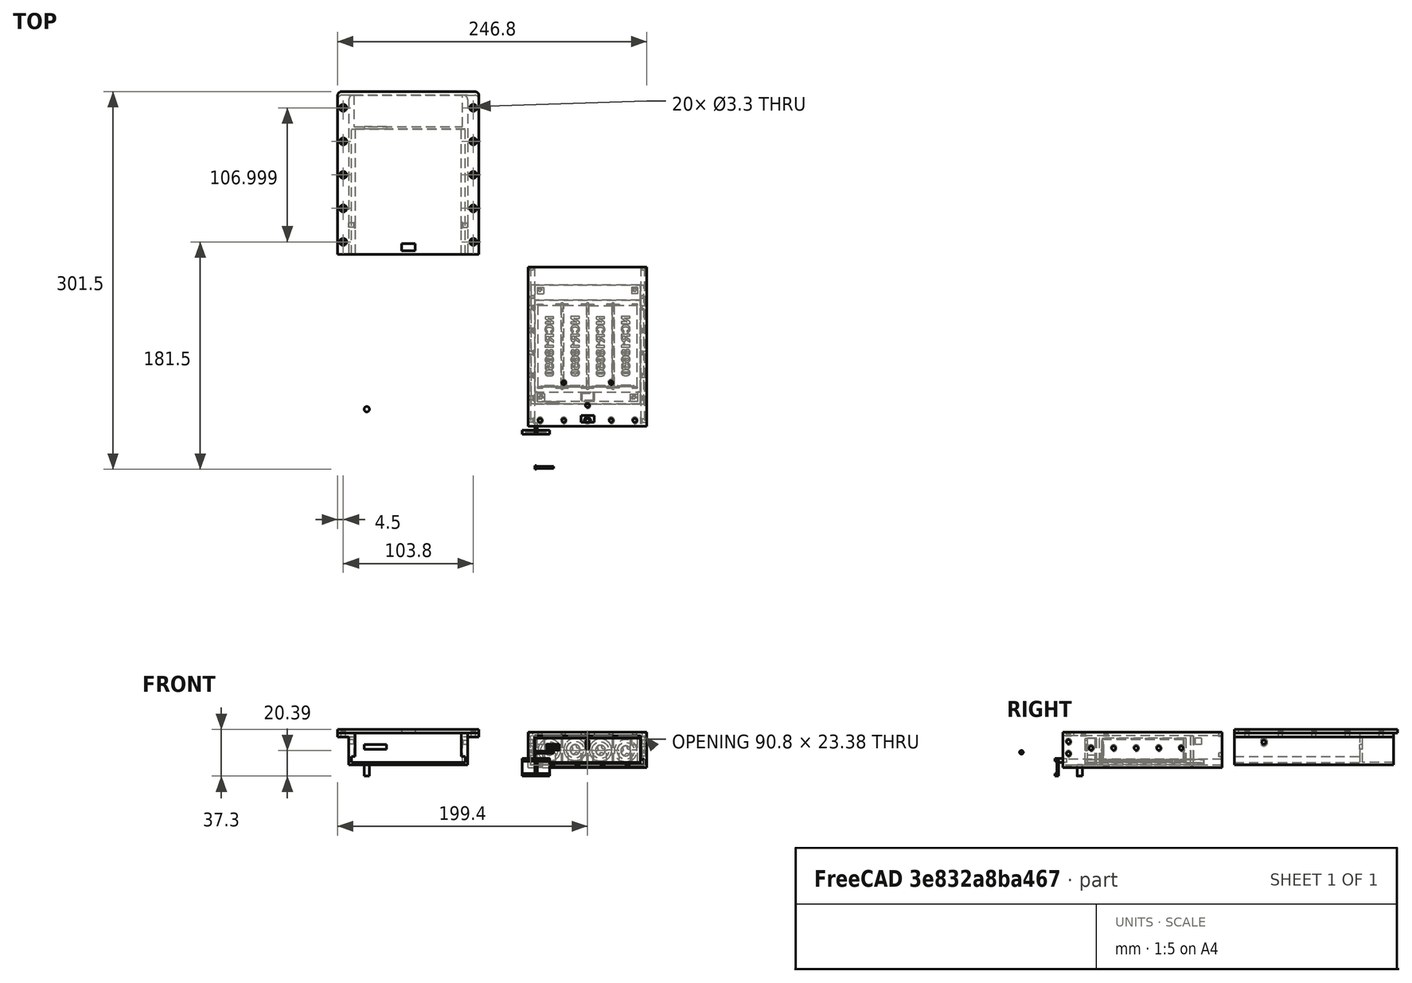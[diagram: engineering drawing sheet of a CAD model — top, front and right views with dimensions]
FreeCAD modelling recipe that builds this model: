
FCSTD DOCUMENT  (FreeCAD 0.21R33771 (Git))
Label: Final Battery Design
License: All rights reserved
LicenseURL: http://en.wikipedia.org/wiki/All_rights_reserved
objects: Sketcher::SketchObject×66, Part::Extrusion×27, App::MeasureDistance×25, PartDesign::Hole×17, PartDesign::Pocket×16, App::Part×14, PartDesign::Body×10, PartDesign::FeatureBase×10, Part::Feature×4, PartDesign::Pad×4, PartDesign::Fillet×3, TechDraw::DrawViewDimension×2, TechDraw::DrawSVGTemplate×1, TechDraw::DrawViewPart×1, TechDraw::DrawPage×1
note: 199 computed .brp shape members not serialized (recipe doc carries the construction recipe); baked Part::Feature solids carry a one-line shape summary decoded from their .brp

FEATURE [Part::Feature] Part__Feature  label="cell 001"
  Placement = pos=(11.67,-30.7,11.73) rot=(1,0,0;1.5708rad)
  shape: bbox 19.48 x 65 x 19.48 mm, 202 faces (baked)
FEATURE [Part::Feature] Part__Feature001  label="cell 002"
  Placement = pos=(32.21,-30.56,12.09) rot=(1,0,0;1.5708rad)
  shape: bbox 19.48 x 65 x 19.48 mm, 202 faces (baked)
FEATURE [Part::Feature] Part__Feature002  label="cell 003"
  Placement = pos=(52.45,-30.79,11.7) rot=(1,0,0;1.5708rad)
  shape: bbox 19.48 x 65 x 19.48 mm, 202 faces (baked)
FEATURE [Part::Feature] Part__Feature003  label="cell 004"
  Placement = pos=(72.58,-30.46,11.13) rot=(1,0,0;1.5708rad)
  shape: bbox 19.48 x 65 x 19.48 mm, 202 faces (baked)
FEATURE [PartDesign::Body] Body  label="CELL MOUNT BODY"
  Origin = -> Origin001
FEATURE [Sketcher::SketchObject] Sketch
  FullyConstrained = false
  MapMode = 5
  Support = -> [XY_Plane001]
  sketch-geometry (4):
    g0: LineSegment StartX=0 StartY=-99.794 StartZ=0 EndX=84.2 EndY=-99.794 EndZ=0
    g1: LineSegment StartX=84.2 StartY=-99.794 StartZ=0 EndX=84.2 EndY=-26.494 EndZ=0
    g2: LineSegment StartX=84.2 StartY=-26.494 StartZ=0 EndX=0 EndY=-26.494 EndZ=0
    g3: LineSegment StartX=0 StartY=-26.494 StartZ=0 EndX=0 EndY=-99.794 EndZ=0
  constraints (10):
    c: Coincident(g0,g1)
    c: Coincident(g1,g2)
    c: Coincident(g2,g3)
    c: Coincident(g3,g0)
    c: Horizontal(g0)
    c: Horizontal(g2)
    c: Vertical(g1)
    c: Vertical(g3)
    c: DistanceX(g2,g2) = 84.2
    c: DistanceY(g3,g3) = 73.3
FEATURE [App::Part] Part001  label="Batt Cells"
  Group = -> [Part__Feature,Part__Feature001,Part__Feature002,Part__Feature003]
  Origin = -> Origin002
FEATURE [Part::Extrusion] Extrude  label="CELL MOUNT FLOOR"
  Base = -> Sketch
  Dir = (0,0,1)
  DirMode = 2
  FaceMakerClass = Part::FaceMakerBullseye
  LengthFwd = 2
  LengthRev = 0
  Solid = true
  Symmetric = false
FEATURE [Sketcher::SketchObject] Sketch001
  FullyConstrained = false
  MapMode = 5
  Placement = pos=(0,0,2) rot=(0,0,1;0rad)
  Support = -> [Extrude]
  sketch-geometry (12):
    g0: LineSegment StartX=0 StartY=-26.494 StartZ=0 EndX=84.2 EndY=-26.494 EndZ=0
    g1: LineSegment StartX=84.2 StartY=-26.494 StartZ=0 EndX=84.2 EndY=-99.794 EndZ=0
    g2: LineSegment StartX=84.2 StartY=-99.794 StartZ=0 EndX=0 EndY=-99.794 EndZ=0
    g3: LineSegment StartX=0 StartY=-99.794 StartZ=0 EndX=0 EndY=-26.494 EndZ=0
    g4: LineSegment StartX=84.2 StartY=-99.794 StartZ=0 EndX=84.2 EndY=-97.79 EndZ=0
    g5: LineSegment StartX=84.2 StartY=-97.79 StartZ=0 EndX=82.2 EndY=-97.79 EndZ=0
    g6: LineSegment StartX=0 StartY=-26.494 StartZ=0 EndX=0 EndY=-28.49 EndZ=0
    g7: LineSegment StartX=0 StartY=-28.49 StartZ=0 EndX=2 EndY=-28.49 EndZ=0
    g8: LineSegment StartX=2 StartY=-28.49 StartZ=0 EndX=82.2 EndY=-28.49 EndZ=0
    g9: LineSegment StartX=82.2 StartY=-28.49 StartZ=0 EndX=82.2 EndY=-97.79 EndZ=0
    g10: LineSegment StartX=82.2 StartY=-97.79 StartZ=0 EndX=2 EndY=-97.79 EndZ=0
    g11: LineSegment StartX=2 StartY=-97.79 StartZ=0 EndX=2 EndY=-28.49 EndZ=0
  constraints (31):
    c: Coincident(g0,g1)
    c: Coincident(g1,g2)
    c: Coincident(g2,g3)
    c: Coincident(g3,g0)
    c: Horizontal(g0)
    c: Horizontal(g2)
    c: Vertical(g1)
    c: Vertical(g3)
    c: PointOnObject(g0,g-2)
    c: DistanceX(g2,g2) = 84.2
    c: DistanceY(g1,g1) = 73.3
    c: Coincident(g4,g1)
    c: PointOnObject(g4,g1)
    c: Coincident(g5,g4)
    c: Horizontal(g5)
    c: Coincident(g6,g0)
    c: PointOnObject(g6,g3)
    c: Coincident(g7,g6)
    c: Horizontal(g7)
    c: Coincident(g8,g9)
    c: Coincident(g9,g10)
    c: Coincident(g10,g11)
    c: Coincident(g11,g8)
    c: Horizontal(g8)
    c: Horizontal(g10)
    c: Vertical(g9)
    c: Vertical(g11)
    c: Coincident(g8,g7)
    c: Coincident(g9,g5)
    c: DistanceX(g8,g8) = 80.2
    c: DistanceY(g9,g9) = 69.3
FEATURE [Part::Extrusion] Extrude001  label="CELL MOUNT EXT WALLS"
  Base = -> Sketch001
  Dir = (0,0,1)
  DirMode = 2
  FaceMakerClass = Part::FaceMakerBullseye
  LengthFwd = 19.3
  LengthRev = 0
  Solid = true
  Symmetric = false
FEATURE [Sketcher::SketchObject] Sketch002
  FullyConstrained = false
  MapMode = 5
  Placement = pos=(0,0,2) rot=(0,0,1;0rad)
  Support = -> [Extrude]
  sketch-geometry (15):
    g0: LineSegment StartX=22.2999 StartY=-28.6 StartZ=0 EndX=41.5999 EndY=-28.6 EndZ=0
    g1: LineSegment StartX=21.2995 StartY=-28.49 StartZ=0 EndX=22.2995 EndY=-28.49 EndZ=0
    g2: LineSegment StartX=22.2995 StartY=-28.49 StartZ=0 EndX=22.2995 EndY=-97.8 EndZ=0
    g3: LineSegment StartX=22.2995 StartY=-97.8 StartZ=0 EndX=21.2995 EndY=-97.8 EndZ=0
    g4: LineSegment StartX=21.2995 StartY=-97.8 StartZ=0 EndX=21.2995 EndY=-28.49 EndZ=0
    g5: LineSegment StartX=41.6 StartY=-28.49 StartZ=0 EndX=42.6 EndY=-28.49 EndZ=0
    g6: LineSegment StartX=42.6 StartY=-28.49 StartZ=0 EndX=42.6 EndY=-97.79 EndZ=0
    g7: LineSegment StartX=42.6 StartY=-97.79 StartZ=0 EndX=41.6 EndY=-97.79 EndZ=0
    g8: LineSegment StartX=41.6 StartY=-97.79 StartZ=0 EndX=41.6 EndY=-28.49 EndZ=0
    g9: LineSegment StartX=42.6 StartY=-28.6021 StartZ=0 EndX=61.9 EndY=-28.6021 EndZ=0
    g10: LineSegment StartX=61.9 StartY=-28.49 StartZ=0 EndX=62.9 EndY=-28.49 EndZ=0
    g11: LineSegment StartX=62.9 StartY=-28.49 StartZ=0 EndX=62.9 EndY=-97.8 EndZ=0
    g12: LineSegment StartX=62.9 StartY=-97.8 StartZ=0 EndX=61.9 EndY=-97.8 EndZ=0
    g13: LineSegment StartX=61.9 StartY=-97.8 StartZ=0 EndX=61.9 EndY=-28.49 EndZ=0
    g14: LineSegment StartX=62.9 StartY=-28.601 StartZ=0 EndX=82.2 EndY=-28.601 EndZ=0
  constraints (38):
    c: Horizontal(g0)
    c: Coincident(g1,g2)
    c: Coincident(g2,g3)
    c: Coincident(g3,g4)
    c: Coincident(g4,g1)
    c: Horizontal(g1)
    c: Horizontal(g3)
    c: Vertical(g2)
    c: Vertical(g4)
    c: Coincident(g5,g6)
    c: Coincident(g6,g7)
    c: Coincident(g7,g8)
    c: Coincident(g8,g5)
    c: Horizontal(g5)
    c: Horizontal(g7)
    c: Vertical(g6)
    c: Vertical(g8)
    c: PointOnObject(g9,g6)
    c: Horizontal(g9)
    c: Coincident(g10,g11)
    c: Coincident(g11,g12)
    c: Coincident(g12,g13)
    c: Coincident(g13,g10)
    c: Horizontal(g10)
    c: Horizontal(g12)
    c: Vertical(g11)
    c: Vertical(g13)
    c: PointOnObject(g14,g11)
    c: Horizontal(g14)
    c: DistanceY(g4,g4) = 69.31
    c: DistanceY(g8,g8) = 69.3
    c: DistanceY(g13,g13) = 69.31
    c: DistanceX(g1,g1) = 1
    c: DistanceX(g0,g0) = 19.3
    c: DistanceX(g9,g9) = 19.3
    c: DistanceX(g5,g5) = 1
    c: DistanceX(g10,g10) = 1
    c: DistanceX(g14,g14) = 19.3
FEATURE [Part::Extrusion] Extrude002  label="CELL DIVIDER WALLS"
  Base = -> Sketch002
  Dir = (0,0,1)
  DirMode = 2
  FaceMakerClass = Part::FaceMakerBullseye
  LengthFwd = 19.3
  LengthRev = 0
  Solid = true
  Symmetric = false
FEATURE [Sketcher::SketchObject] Sketch003
  FullyConstrained = false
  MapMode = 5
  Placement = pos=(0,0,2) rot=(0,0,1;0rad)
  Support = -> [Extrude]
  sketch-geometry (66):
    g0: LineSegment StartX=2.1 StartY=-28.49 StartZ=0 EndX=2.1 EndY=-29.49 EndZ=0
    g1: LineSegment StartX=2 StartY=-29.5 StartZ=0 EndX=6.5 EndY=-29.5 EndZ=0
    g2: LineSegment StartX=6.5 StartY=-29.5 StartZ=0 EndX=6.5 EndY=-30.5 EndZ=0
    g3: LineSegment StartX=6.5 StartY=-30.5 StartZ=0 EndX=2 EndY=-30.5 EndZ=0
    g4: LineSegment StartX=2 StartY=-30.5 StartZ=0 EndX=2 EndY=-29.5 EndZ=0
    g5: LineSegment StartX=21.3 StartY=-29.49 StartZ=0 EndX=16.8 EndY=-29.49 EndZ=0
    g6: LineSegment StartX=16.8 StartY=-29.49 StartZ=0 EndX=16.8 EndY=-30.49 EndZ=0
    g7: LineSegment StartX=16.8 StartY=-30.49 StartZ=0 EndX=21.3 EndY=-30.49 EndZ=0
    g8: LineSegment StartX=21.3 StartY=-30.49 StartZ=0 EndX=21.3 EndY=-29.49 EndZ=0
    g9: LineSegment StartX=22.3 StartY=-30.49 StartZ=0 EndX=26.8 EndY=-30.49 EndZ=0
    g10: LineSegment StartX=26.8 StartY=-30.49 StartZ=0 EndX=26.8 EndY=-29.49 EndZ=0
    g11: LineSegment StartX=26.8 StartY=-29.49 StartZ=0 EndX=22.3 EndY=-29.49 EndZ=0
    g12: LineSegment StartX=22.3 StartY=-29.49 StartZ=0 EndX=22.3 EndY=-30.49 EndZ=0
    g13: LineSegment StartX=41.6 StartY=-29.5 StartZ=0 EndX=37.1 EndY=-29.5 EndZ=0
    g14: LineSegment StartX=37.1 StartY=-29.5 StartZ=0 EndX=37.1 EndY=-30.5 EndZ=0
    g15: LineSegment StartX=37.1 StartY=-30.5 StartZ=0 EndX=41.6 EndY=-30.5 EndZ=0
    g16: LineSegment StartX=41.6 StartY=-30.5 StartZ=0 EndX=41.6 EndY=-29.5 EndZ=0
    g17: LineSegment StartX=42.6 StartY=-29.5 StartZ=0 EndX=47.1 EndY=-29.5 EndZ=0
    g18: LineSegment StartX=47.1 StartY=-29.5 StartZ=0 EndX=47.1 EndY=-30.5 EndZ=0
    g19: LineSegment StartX=47.1 StartY=-30.5 StartZ=0 EndX=42.6 EndY=-30.5 EndZ=0
    g20: LineSegment StartX=42.6 StartY=-30.5 StartZ=0 EndX=42.6 EndY=-29.5 EndZ=0
    g21: LineSegment StartX=61.9 StartY=-29.5 StartZ=0 EndX=57.4 EndY=-29.5 EndZ=0
    g22: LineSegment StartX=57.4 StartY=-29.5 StartZ=0 EndX=57.4 EndY=-30.5 EndZ=0
    g23: LineSegment StartX=57.4 StartY=-30.5 StartZ=0 EndX=61.9 EndY=-30.5 EndZ=0
    g24: LineSegment StartX=61.9 StartY=-30.5 StartZ=0 EndX=61.9 EndY=-29.5 EndZ=0
    g25: LineSegment StartX=62.9 StartY=-29.5 StartZ=0 EndX=67.4 EndY=-29.5 EndZ=0
    g26: LineSegment StartX=67.4 StartY=-29.5 StartZ=0 EndX=67.4 EndY=-30.5 EndZ=0
    g27: LineSegment StartX=67.4 StartY=-30.5 StartZ=0 EndX=62.9 EndY=-30.5 EndZ=0
    g28: LineSegment StartX=62.9 StartY=-30.5 StartZ=0 EndX=62.9 EndY=-29.5 EndZ=0
    g29: LineSegment StartX=82.2 StartY=-29.5 StartZ=0 EndX=77.7 EndY=-29.5 EndZ=0
    g30: LineSegment StartX=77.7 StartY=-29.5 StartZ=0 EndX=77.7 EndY=-30.5 EndZ=0
    g31: LineSegment StartX=77.7 StartY=-30.5 StartZ=0 EndX=82.2 EndY=-30.5 EndZ=0
    g32: LineSegment StartX=82.2 StartY=-30.5 StartZ=0 EndX=82.2 EndY=-29.5 EndZ=0
    g33: LineSegment StartX=2.1 StartY=-97.79 StartZ=0 EndX=2.1 EndY=-96.7 EndZ=0
    g34: LineSegment StartX=2 StartY=-96.7 StartZ=0 EndX=6.5 EndY=-96.7 EndZ=0
    g35: LineSegment StartX=6.5 StartY=-96.7 StartZ=0 EndX=6.5 EndY=-95.7 EndZ=0
    g36: LineSegment StartX=6.5 StartY=-95.7 StartZ=0 EndX=2 EndY=-95.7 EndZ=0
    g37: LineSegment StartX=2 StartY=-95.7 StartZ=0 EndX=2 EndY=-96.7 EndZ=0
    g38: LineSegment StartX=21.3 StartY=-95.7 StartZ=0 EndX=16.8 EndY=-95.7 EndZ=0
    g39: LineSegment StartX=16.8 StartY=-95.7 StartZ=0 EndX=16.8 EndY=-96.7 EndZ=0
    g40: LineSegment StartX=16.8 StartY=-96.7 StartZ=0 EndX=21.3 EndY=-96.7 EndZ=0
    g41: LineSegment StartX=21.3 StartY=-96.7 StartZ=0 EndX=21.3 EndY=-95.7 EndZ=0
    g42: LineSegment StartX=22.3 StartY=-96.7 StartZ=0 EndX=26.8 EndY=-96.7 EndZ=0
    g43: LineSegment StartX=26.8 StartY=-96.7 StartZ=0 EndX=26.8 EndY=-95.7 EndZ=0
    g44: LineSegment StartX=26.8 StartY=-95.7 StartZ=0 EndX=22.3 EndY=-95.7 EndZ=0
    g45: LineSegment StartX=22.3 StartY=-95.7 StartZ=0 EndX=22.3 EndY=-96.7 EndZ=0
    g46: LineSegment StartX=41.6 StartY=-95.7 StartZ=0 EndX=37.1 EndY=-95.7 EndZ=0
    g47: LineSegment StartX=37.1 StartY=-95.7 StartZ=0 EndX=37.1 EndY=-96.7 EndZ=0
    g48: LineSegment StartX=37.1 StartY=-96.7 StartZ=0 EndX=41.6 EndY=-96.7 EndZ=0
    g49: LineSegment StartX=41.6 StartY=-96.7 StartZ=0 EndX=41.6 EndY=-95.7 EndZ=0
    g50: LineSegment StartX=42.6 StartY=-96.7 StartZ=0 EndX=47.1 EndY=-96.7 EndZ=0
    g51: LineSegment StartX=47.1 StartY=-96.7 StartZ=0 EndX=47.1 EndY=-95.7 EndZ=0
    g52: LineSegment StartX=47.1 StartY=-95.7 StartZ=0 EndX=42.6 EndY=-95.7 EndZ=0
    g53: LineSegment StartX=42.6 StartY=-95.7 StartZ=0 EndX=42.6 EndY=-96.7 EndZ=0
    g54: LineSegment StartX=61.9 StartY=-95.7 StartZ=0 EndX=57.4 EndY=-95.7 EndZ=0
    g55: LineSegment StartX=57.4 StartY=-95.7 StartZ=0 EndX=57.4 EndY=-96.7 EndZ=0
    g56: LineSegment StartX=57.4 StartY=-96.7 StartZ=0 EndX=61.9 EndY=-96.7 EndZ=0
    g57: LineSegment StartX=61.9 StartY=-96.7 StartZ=0 EndX=61.9 EndY=-95.7 EndZ=0
    g58: LineSegment StartX=62.9 StartY=-95.7 StartZ=0 EndX=67.4 EndY=-95.7 EndZ=0
    g59: LineSegment StartX=67.4 StartY=-95.7 StartZ=0 EndX=67.4 EndY=-96.7 EndZ=0
    g60: LineSegment StartX=67.4 StartY=-96.7 StartZ=0 EndX=62.9 EndY=-96.7 EndZ=0
    g61: LineSegment StartX=62.9 StartY=-96.7 StartZ=0 EndX=62.9 EndY=-95.7 EndZ=0
    g62: LineSegment StartX=82.2 StartY=-95.7 StartZ=0 EndX=77.7 EndY=-95.7 EndZ=0
    g63: LineSegment StartX=77.7 StartY=-95.7 StartZ=0 EndX=77.7 EndY=-96.7 EndZ=0
    g64: LineSegment StartX=77.7 StartY=-96.7 StartZ=0 EndX=82.2 EndY=-96.7 EndZ=0
    g65: LineSegment StartX=82.2 StartY=-96.7 StartZ=0 EndX=82.2 EndY=-95.7 EndZ=0
  constraints (162):
    c: Vertical(g0)
    c: Coincident(g1,g2)
    c: Coincident(g2,g3)
    c: Coincident(g3,g4)
    c: Coincident(g4,g1)
    c: Horizontal(g1)
    c: Horizontal(g3)
    c: Vertical(g2)
    c: Vertical(g4)
    c: Coincident(g5,g6)
    c: Coincident(g6,g7)
    c: Coincident(g7,g8)
    c: Coincident(g8,g5)
    c: Horizontal(g5)
    c: Horizontal(g7)
    c: Vertical(g6)
    c: Vertical(g8)
    c: DistanceX(g1,g1) = 4.5
    c: DistanceX(g5,g5) = 4.5
    c: DistanceY(g2,g2) = 1
    c: DistanceY(g6,g6) = 1
    c: Coincident(g9,g10)
    c: Coincident(g10,g11)
    c: Coincident(g11,g12)
    c: Coincident(g12,g9)
    c: Horizontal(g9)
    c: Horizontal(g11)
    c: Vertical(g10)
    c: Vertical(g12)
    c: Coincident(g13,g14)
    c: Coincident(g14,g15)
    c: Coincident(g15,g16)
    c: Coincident(g16,g13)
    c: Horizontal(g13)
    c: Horizontal(g15)
    c: Vertical(g14)
    c: Vertical(g16)
    c: DistanceX(g13,g13) = 4.5
    c: DistanceX(g11,g11) = 4.5
    c: DistanceY(g10,g10) = 1
    c: DistanceY(g14,g14) = 1
    c: Coincident(g17,g18)
    c: Coincident(g18,g19)
    c: Coincident(g19,g20)
    c: Coincident(g20,g17)
    c: Horizontal(g17)
    c: Horizontal(g19)
    c: Vertical(g18)
    c: Vertical(g20)
    c: Coincident(g21,g22)
    c: Coincident(g22,g23)
    c: Coincident(g23,g24)
    c: Coincident(g24,g21)
    c: Horizontal(g21)
    c: Horizontal(g23)
    c: Vertical(g22)
    c: Vertical(g24)
    c: DistanceX(g17,g17) = 4.5
    c: DistanceY(g18,g18) = 1
    c: DistanceX(g21,g21) = 4.5
    c: DistanceY(g22,g22) = 1
    c: Coincident(g25,g26)
    c: Coincident(g26,g27)
    c: Coincident(g27,g28)
    c: Coincident(g28,g25)
    c: Horizontal(g25)
    c: Horizontal(g27)
    c: Vertical(g26)
    c: Vertical(g28)
    c: Coincident(g29,g30)
    c: Coincident(g30,g31)
    c: Coincident(g31,g32)
    c: Coincident(g32,g29)
    c: Horizontal(g29)
    c: Horizontal(g31)
    c: Vertical(g30)
    c: Vertical(g32)
    c: DistanceX(g29,g29) = 4.5
    c: DistanceX(g25,g25) = 4.5
    c: DistanceY(g26,g26) = 1
    c: DistanceY(g30,g30) = 1
    c: Vertical(g33)
    c: Coincident(g34,g35)
    c: Coincident(g35,g36)
    c: Coincident(g36,g37)
    c: Coincident(g37,g34)
    c: Horizontal(g34)
    c: Horizontal(g36)
    c: Vertical(g35)
    c: Vertical(g37)
    c: Coincident(g38,g39)
    c: Coincident(g39,g40)
    c: Coincident(g40,g41)
    c: Coincident(g41,g38)
    c: Horizontal(g38)
    c: Horizontal(g40)
    c: Vertical(g39)
    c: Vertical(g41)
    c: DistanceY(g39,g39) = 1
    c: DistanceY(g35,g35) = 1
    c: DistanceX(g36,g36) = 4.5
    c: DistanceX(g38,g38) = 4.5
    c: Coincident(g42,g43)
    c: Coincident(g43,g44)
    c: Coincident(g44,g45)
    c: Coincident(g45,g42)
    c: Horizontal(g42)
    c: Horizontal(g44)
    c: Vertical(g43)
    c: Vertical(g45)
    c: Coincident(g46,g47)
    c: Coincident(g47,g48)
    c: Coincident(g48,g49)
    c: Coincident(g49,g46)
    c: Horizontal(g46)
    c: Horizontal(g48)
    c: Vertical(g47)
    c: Vertical(g49)
    c: DistanceX(g46,g46) = 4.5
    c: DistanceX(g44,g44) = 4.5
    c: DistanceY(g43,g43) = 1
    c: DistanceY(g47,g47) = 1
    c: Coincident(g50,g51)
    c: Coincident(g51,g52)
    c: Coincident(g52,g53)
    c: Coincident(g53,g50)
    c: Horizontal(g50)
    c: Horizontal(g52)
    c: Vertical(g51)
    c: Vertical(g53)
    c: DistanceY(g51,g51) = 1
    c: DistanceX(g52,g52) = 4.5
    c: Coincident(g54,g55)
    c: Coincident(g55,g56)
    c: Coincident(g56,g57)
    c: Coincident(g57,g54)
    c: Horizontal(g54)
    c: Horizontal(g56)
    c: Vertical(g55)
    c: Vertical(g57)
    c: DistanceX(g54,g54) = 4.5
    c: DistanceY(g55,g55) = 1
    c: Coincident(g58,g59)
    c: Coincident(g59,g60)
    c: Coincident(g60,g61)
    c: Coincident(g61,g58)
    c: Horizontal(g58)
    c: Horizontal(g60)
    c: Vertical(g59)
    c: Vertical(g61)
    c: DistanceY(g59,g59) = 1
    c: DistanceX(g60,g60) = 4.5
    c: Coincident(g62,g63)
    c: Coincident(g63,g64)
    c: Coincident(g64,g65)
    c: Coincident(g65,g62)
    c: Horizontal(g62)
    c: Horizontal(g64)
    c: Vertical(g63)
    c: Vertical(g65)
    c: DistanceY(g63,g63) = 1
    c: DistanceX(g62,g62) = 4.5
FEATURE [Part::Extrusion] Extrude003  label="CELL ENDS SPRING HOLDERS"
  Base = -> Sketch003
  Dir = (0,0,1)
  DirMode = 2
  FaceMakerClass = Part::FaceMakerBullseye
  LengthFwd = 9.65
  LengthRev = 0
  Solid = true
  Symmetric = false
FEATURE [Sketcher::SketchObject] Sketch006
  FullyConstrained = false
  MapMode = 5
  Support = -> [XY_Plane001]
  sketch-geometry (4):
    g0: LineSegment StartX=0 StartY=-26.49 StartZ=0 EndX=84.2 EndY=-26.49 EndZ=0
    g1: LineSegment StartX=84.2 StartY=-26.49 StartZ=0 EndX=84.2 EndY=-14.4 EndZ=0
    g2: LineSegment StartX=84.2 StartY=-14.4 StartZ=0 EndX=0 EndY=-14.4 EndZ=0
    g3: LineSegment StartX=0 StartY=-14.4 StartZ=0 EndX=0 EndY=-26.49 EndZ=0
  constraints (11):
    c: Coincident(g0,g1)
    c: Coincident(g1,g2)
    c: Coincident(g2,g3)
    c: Coincident(g3,g0)
    c: Horizontal(g0)
    c: Horizontal(g2)
    c: Vertical(g1)
    c: Vertical(g3)
    c: PointOnObject(g0,g-2)
    c: DistanceX(g2,g2) = 84.2
    c: DistanceY(g1,g1) = 12.09
FEATURE [Part::Extrusion] Extrude004  label="BACK FLOOR"
  Base = -> Sketch006
  Dir = (0,0,1)
  DirMode = 2
  FaceMakerClass = Part::FaceMakerBullseye
  LengthFwd = 2
  LengthRev = 0
  Solid = true
  Symmetric = false
FEATURE [Sketcher::SketchObject] Sketch007
  FullyConstrained = false
  MapMode = 5
  Placement = pos=(0,0,2) rot=(0,0,1;0rad)
  Support = -> [Extrude004]
  sketch-geometry (8):
    g0: LineSegment StartX=0 StartY=-26.4942 StartZ=0 EndX=84.2 EndY=-26.4942 EndZ=0
    g1: LineSegment StartX=84.2 StartY=-26.4942 StartZ=0 EndX=84.2 EndY=-14.4 EndZ=0
    g2: LineSegment StartX=84.2 StartY=-14.4 StartZ=0 EndX=0 EndY=-14.4 EndZ=0
    g3: LineSegment StartX=0 StartY=-14.4 StartZ=0 EndX=0 EndY=-26.4942 EndZ=0
    g4: LineSegment StartX=82.2 StartY=-26.4942 StartZ=0 EndX=2 EndY=-26.4942 EndZ=0
    g5: LineSegment StartX=2 StartY=-26.4942 StartZ=0 EndX=2 EndY=-16.37 EndZ=0
    g6: LineSegment StartX=2 StartY=-16.37 StartZ=0 EndX=82.2 EndY=-16.37 EndZ=0
    g7: LineSegment StartX=82.2 StartY=-16.37 StartZ=0 EndX=82.2 EndY=-26.4942 EndZ=0
  constraints (22):
    c: Coincident(g0,g1)
    c: Coincident(g1,g2)
    c: Coincident(g2,g3)
    c: Coincident(g3,g0)
    c: Horizontal(g0)
    c: Horizontal(g2)
    c: Vertical(g1)
    c: Vertical(g3)
    c: PointOnObject(g0,g-2)
    c: Coincident(g4,g5)
    c: Coincident(g5,g6)
    c: Coincident(g6,g7)
    c: Coincident(g7,g4)
    c: Horizontal(g4)
    c: Horizontal(g6)
    c: Vertical(g5)
    c: Vertical(g7)
    c: PointOnObject(g4,g0)
    c: DistanceX(g6,g6) = 80.2
    c: DistanceX(g2,g2) = 84.2
    c: DistanceY(g5,g5) = 10.1242
    c: DistanceY(g3,g3) = 12.0942
FEATURE [Part::Extrusion] Extrude005
  Base = -> Sketch007
  Dir = (0,0,1)
  DirMode = 2
  FaceMakerClass = Part::FaceMakerBullseye
  LengthFwd = 19.3
  LengthRev = 0
  Solid = true
  Symmetric = false
FEATURE [PartDesign::Body] Body001  label="BACK BODY"
  Origin = -> Origin003
FEATURE [Sketcher::SketchObject] Sketch011
  FullyConstrained = false
  MapMode = 5
  Support = -> [XY_Plane005]
  sketch-geometry (4):
    g0: LineSegment StartX=-140 StartY=-110 StartZ=0 EndX=-128 EndY=-110 EndZ=0
    g1: LineSegment StartX=-128 StartY=-110 StartZ=0 EndX=-128 EndY=-117 EndZ=0
    g2: LineSegment StartX=-128 StartY=-117 StartZ=0 EndX=-140 EndY=-117 EndZ=0
    g3: LineSegment StartX=-140 StartY=-117 StartZ=0 EndX=-140 EndY=-110 EndZ=0
  constraints (10):
    c: Coincident(g0,g1)
    c: Coincident(g1,g2)
    c: Coincident(g2,g3)
    c: Coincident(g3,g0)
    c: Horizontal(g0)
    c: Horizontal(g2)
    c: Vertical(g1)
    c: Vertical(g3)
    c: DistanceX(g0,g0) = 12
    c: DistanceY(g3,g3) = 7
FEATURE [Part::Extrusion] Extrude007
  Base = -> Sketch011
  Dir = (0,0,1)
  DirMode = 2
  FaceMakerClass = Part::FaceMakerBullseye
  LengthFwd = 7
  LengthRev = 0
  Solid = true
  Symmetric = false
FEATURE [Sketcher::SketchObject] Sketch012
  FullyConstrained = false
  MapMode = 5
  Placement = pos=(0,0,7) rot=(0,0,1;0rad)
  Support = -> [Extrude007]
  sketch-geometry (4):
    g0: LineSegment StartX=-139 StartY=-111 StartZ=0 EndX=-129 EndY=-111 EndZ=0
    g1: LineSegment StartX=-129 StartY=-111 StartZ=0 EndX=-129 EndY=-116 EndZ=0
    g2: LineSegment StartX=-129 StartY=-116 StartZ=0 EndX=-139 EndY=-116 EndZ=0
    g3: LineSegment StartX=-139 StartY=-116 StartZ=0 EndX=-139 EndY=-111 EndZ=0
  constraints (10):
    c: Coincident(g0,g1)
    c: Coincident(g1,g2)
    c: Coincident(g2,g3)
    c: Coincident(g3,g0)
    c: Horizontal(g0)
    c: Horizontal(g2)
    c: Vertical(g1)
    c: Vertical(g3)
    c: DistanceY(g3,g3) = 5
    c: DistanceX(g0,g0) = 10
FEATURE [Sketcher::SketchObject] Sketch015
  FullyConstrained = false
  MapMode = 5
  Placement = pos=(0,-117,0) rot=(1,0,0;1.5708rad)
  Support = -> [Extrude007]
  sketch-geometry (4):
    g0: LineSegment StartX=-135 StartY=2 StartZ=0 EndX=-133 EndY=2 EndZ=0
    g1: LineSegment StartX=-133 StartY=2 StartZ=0 EndX=-133 EndY=5 EndZ=0
    g2: LineSegment StartX=-133 StartY=5 StartZ=0 EndX=-135 EndY=5 EndZ=0
    g3: LineSegment StartX=-135 StartY=5 StartZ=0 EndX=-135 EndY=2 EndZ=0
  constraints (10):
    c: Coincident(g0,g1)
    c: Coincident(g1,g2)
    c: Coincident(g2,g3)
    c: Coincident(g3,g0)
    c: Horizontal(g0)
    c: Horizontal(g2)
    c: Vertical(g1)
    c: Vertical(g3)
    c: DistanceX(g2,g2) = 2
    c: DistanceY(g3,g3) = 3
FEATURE [PartDesign::FeatureBase] BaseFeature002
  BaseFeature = -> Extrude007
FEATURE [PartDesign::Pocket] Pocket002
  Direction = (0,1,-2e-16)
  Length = 3.5
  Length2 = 5
  Profile = -> Sketch015
  ReferenceAxis = -> Sketch015 [N_Axis]
  Type = 0
FEATURE [Sketcher::SketchObject] Sketch016
  FullyConstrained = false
  MapMode = 5
  Placement = pos=(-128,0,0) rot=(0.57735,0.57735,0.57735;2.0944rad)
  Support = -> [Pocket002]
  sketch-geometry (1):
    g0: Circle CenterX=-115.25 CenterY=3.5 CenterZ=0 NormalX=0 NormalY=0 NormalZ=1 AngleXU=0 Radius=0.75
  constraints (1):
    c: Diameter(g0) = 1.5
FEATURE [PartDesign::FeatureBase] BaseFeature003
  BaseFeature = -> Pocket002
FEATURE [PartDesign::Hole] Hole  label="MAIN LOCKING HANDLE MNT"
  CustomThreadClearance = 0
  Depth = 12
  DepthType = 0
  Diameter = 1.5
  DrillForDepth = false
  DrillPoint = 1
  DrillPointAngle = 118
  HoleCutCountersinkAngle = 90
  HoleCutCustomValues = false
  HoleCutDepth = 0
  HoleCutDiameter = 6.1
  HoleCutType = 0
  ModelThread = false
  Profile = -> Sketch016
  Tapered = false
  TaperedAngle = 90
  ThreadClass = 0
  ThreadDepth = 12
  ThreadDepthType = 0
  ThreadDirection = 0
  ThreadFit = 0
  ThreadSize = 0
  ThreadType = 0
  Threaded = false
  UseCustomThreadClearance = false
FEATURE [PartDesign::Body] Body003  label="HANDLE LOCK"
  Origin = -> Origin007
FEATURE [Sketcher::SketchObject] Sketch017
  FullyConstrained = false
  MapMode = 5
  Placement = pos=(0,0,0) rot=(0.57735,0.57735,0.57735;2.0944rad)
  Support = -> [YZ_Plane007]
  sketch-geometry (17):
    g0: LineSegment StartX=-128 StartY=5 StartZ=0 EndX=-130 EndY=5 EndZ=0
    g1: LineSegment StartX=-130 StartY=5 StartZ=0 EndX=-130.3 EndY=5 EndZ=0
    g2: LineSegment StartX=-130.3 StartY=5 StartZ=0 EndX=-133.3 EndY=5 EndZ=0
    g3: LineSegment StartX=-133.3 StartY=5 StartZ=0 EndX=-133.3 EndY=3 EndZ=0
    g4: LineSegment StartX=-133.3 StartY=3 StartZ=0 EndX=-131.8 EndY=3 EndZ=0
    g5: LineSegment StartX=-131.8 StartY=3 StartZ=0 EndX=-131.8 EndY=-7 EndZ=0
    g6: LineSegment StartX=-131.8 StartY=-7 StartZ=0 EndX=-133.3 EndY=-7 EndZ=0
    g7: LineSegment StartX=-133.3 StartY=-7 StartZ=0 EndX=-133.3 EndY=-9 EndZ=0
    g8: LineSegment StartX=-133.3 StartY=-9 StartZ=0 EndX=-130.3 EndY=-9 EndZ=0
    g9: LineSegment StartX=-128 StartY=5 StartZ=0 EndX=-127.7 EndY=5 EndZ=0
    g10: LineSegment StartX=-127.7 StartY=5 StartZ=0 EndX=-124.2 EndY=5 EndZ=0
    g11: LineSegment StartX=-124.2 StartY=5 StartZ=0 EndX=-124.2 EndY=2 EndZ=0
    g12: LineSegment StartX=-124.2 StartY=2 StartZ=0 EndX=-127.7 EndY=2 EndZ=0
    g13: LineSegment StartX=-127.7 StartY=2 StartZ=0 EndX=-128 EndY=2 EndZ=0
    g14: LineSegment StartX=-128 StartY=2 StartZ=0 EndX=-130 EndY=2 EndZ=0
    g15: LineSegment StartX=-130 StartY=2 StartZ=0 EndX=-130.3 EndY=2 EndZ=0
    g16: LineSegment StartX=-130.3 StartY=2 StartZ=0 EndX=-130.3 EndY=-9 EndZ=0
  constraints (49):
    c: Horizontal(g0)
    c: Coincident(g0,g1)
    c: Horizontal(g1)
    c: Coincident(g1,g2)
    c: Horizontal(g2)
    c: Coincident(g2,g3)
    c: Vertical(g3)
    c: Coincident(g3,g4)
    c: Horizontal(g4)
    c: Coincident(g4,g5)
    c: Vertical(g5)
    c: Coincident(g5,g6)
    c: Horizontal(g6)
    c: Coincident(g6,g7)
    c: Vertical(g7)
    c: Coincident(g7,g8)
    c: Horizontal(g8)
    c: DistanceY(g5,g5) = 10
    c: DistanceY(g3,g3) = 2
    c: DistanceX(g4,g4) = 1.5
    c: DistanceX(g2,g2) = 3
    c: DistanceX(g1,g1) = 0.3
    c: DistanceX(g0,g0) = 2
    c: DistanceX(g6,g6) = 1.5
    c: Coincident(g9,g0)
    c: Horizontal(g9)
    c: Coincident(g9,g10)
    c: Horizontal(g10)
    c: Coincident(g10,g11)
    c: Vertical(g11)
    c: Coincident(g11,g12)
    c: Horizontal(g12)
    c: Coincident(g12,g13)
    c: Horizontal(g13)
    c: Coincident(g13,g14)
    c: Horizontal(g14)
    c: Coincident(g15,g14)
    c: Horizontal(g15)
    c: Coincident(g15,g16)
    c: Coincident(g16,g8)
    c: Vertical(g16)
    c: DistanceY(g7,g7) = 2
    c: DistanceY(g16,g16) = 11
    c: DistanceX(g8,g8) = 3
    c: DistanceX(g15,g15) = 0.3
    c: DistanceX(g14,g14) = 2
    c: DistanceX(g13,g13) = 0.3
    c: DistanceX(g12,g12) = 3.5
    c: DistanceX(g10,g10) = 3.5
FEATURE [PartDesign::Body] Body004  label="HANDLE FASTEN PIN BODY"
  Origin = -> Origin009
FEATURE [Sketcher::SketchObject] Sketch019
  FullyConstrained = false
  MapMode = 5
  Placement = pos=(0,0,0) rot=(0.57735,0.57735,0.57735;2.0944rad)
  Support = -> [YZ_Plane009]
  sketch-geometry (1):
    g0: Circle CenterX=-160 CenterY=10 CenterZ=0 NormalX=0 NormalY=0 NormalZ=1 AngleXU=0 Radius=1.5
  constraints (1):
    c: Diameter(g0) = 3
FEATURE [Part::Extrusion] Extrude011  label="PIN BASE"
  Base = -> Sketch019
  Dir = (1,-1e-16,1e-16)
  DirMode = 2
  FaceMakerClass = Part::FaceMakerBullseye
  LengthFwd = 1.5
  LengthRev = 0
  Solid = true
  Symmetric = false
FEATURE [Sketcher::SketchObject] Sketch020
  FullyConstrained = false
  MapMode = 5
  Placement = pos=(1.5,-3e-16,3e-16) rot=(0.57735,0.57735,0.57735;2.0944rad)
  Support = -> [Extrude011]
  sketch-geometry (1):
    g0: Circle CenterX=-160 CenterY=10 CenterZ=0 NormalX=0 NormalY=0 NormalZ=1 AngleXU=0 Radius=0.74
  constraints (1):
    c: Diameter(g0) = 1.48
FEATURE [Part::Extrusion] Extrude012  label="PIN LENGTH"
  Base = -> Sketch020
  Dir = (1,-2e-16,2e-16)
  DirMode = 2
  FaceMakerClass = Part::FaceMakerBullseye
  LengthFwd = 13.5
  LengthRev = 0
  Solid = true
  Symmetric = false
FEATURE [App::Part] Part004  label="handle to mechanism pin"
  Group = -> [Body004,Sketch019,Extrude011,Sketch020,Extrude012]
  Origin = -> Origin008
  Placement = pos=(34.67,54.77,7.74) rot=(0,0,1;0rad)
FEATURE [Sketcher::SketchObject] Sketch021
  FullyConstrained = false
  MapMode = 5
  Support = -> [XY_Plane010]
  sketch-geometry (4):
    g0: LineSegment StartX=0 StartY=-99.794 StartZ=0 EndX=84.2 EndY=-99.794 EndZ=0
    g1: LineSegment StartX=84.2 StartY=-99.794 StartZ=0 EndX=84.2 EndY=-109.304 EndZ=0
    g2: LineSegment StartX=84.2 StartY=-109.304 StartZ=0 EndX=0 EndY=-109.304 EndZ=0
    g3: LineSegment StartX=0 StartY=-109.304 StartZ=0 EndX=0 EndY=-99.794 EndZ=0
  constraints (11):
    c: Coincident(g0,g1)
    c: Coincident(g1,g2)
    c: Coincident(g2,g3)
    c: Coincident(g3,g0)
    c: Horizontal(g0)
    c: Horizontal(g2)
    c: Vertical(g1)
    c: Vertical(g3)
    c: PointOnObject(g0,g-2)
    c: DistanceX(g2,g2) = 84.2
    c: DistanceY(g1,g1) = 9.51
FEATURE [Part::Extrusion] Extrude013
  Base = -> Sketch021
  Dir = (0,0,1)
  DirMode = 2
  FaceMakerClass = Part::FaceMakerBullseye
  LengthFwd = 2
  LengthRev = 0
  Solid = true
  Symmetric = false
FEATURE [Sketcher::SketchObject] Sketch022
  FullyConstrained = false
  MapMode = 5
  Placement = pos=(0,0,2) rot=(0,0,1;0rad)
  Support = -> [Extrude013]
  sketch-geometry (8):
    g0: LineSegment StartX=0 StartY=-99.8 StartZ=0 EndX=0 EndY=-109.3 EndZ=0
    g1: LineSegment StartX=0 StartY=-109.3 StartZ=0 EndX=84.2 EndY=-109.3 EndZ=0
    g2: LineSegment StartX=84.2 StartY=-109.3 StartZ=0 EndX=84.2 EndY=-99.79 EndZ=0
    g3: LineSegment StartX=84.2 StartY=-99.79 StartZ=0 EndX=82.2 EndY=-99.79 EndZ=0
    g4: LineSegment StartX=82.2 StartY=-99.79 StartZ=0 EndX=82.2 EndY=-107.3 EndZ=0
    g5: LineSegment StartX=82.2 StartY=-107.3 StartZ=0 EndX=2 EndY=-107.3 EndZ=0
    g6: LineSegment StartX=2 StartY=-107.3 StartZ=0 EndX=2 EndY=-99.8 EndZ=0
    g7: LineSegment StartX=2 StartY=-99.8 StartZ=0 EndX=0 EndY=-99.8 EndZ=0
  constraints (23):
    c: PointOnObject(g0,g-2)
    c: PointOnObject(g0,g-2)
    c: Coincident(g0,g1)
    c: Horizontal(g1)
    c: Coincident(g1,g2)
    c: Vertical(g2)
    c: Coincident(g2,g3)
    c: Horizontal(g3)
    c: Coincident(g3,g4)
    c: Vertical(g4)
    c: Coincident(g4,g5)
    c: Horizontal(g5)
    c: Coincident(g5,g6)
    c: Vertical(g6)
    c: Coincident(g6,g7)
    c: Coincident(g7,g0)
    c: Horizontal(g7)
    c: DistanceX(g7,g7) = 2
    c: DistanceX(g1,g1) = 84.2
    c: DistanceX(g5,g5) = 80.2
    c: DistanceY(g2,g2) = 9.51
    c: DistanceY(g4,g4) = 7.51
    c: DistanceY(g6,g6) = 7.5
FEATURE [PartDesign::FeatureBase] BaseFeature005  label="FRONT FLOOR"
  BaseFeature = -> Extrude013
FEATURE [Part::Extrusion] Extrude014  label="FRONT WALL"
  Base = -> Sketch022
  Dir = (0,0,1)
  DirMode = 2
  FaceMakerClass = Part::FaceMakerBullseye
  LengthFwd = 19.3
  LengthRev = 0
  Solid = true
  Symmetric = false
FEATURE [Sketcher::SketchObject] Sketch023
  FullyConstrained = false
  MapMode = 5
  Placement = pos=(0,0,2) rot=(0,0,1;0rad)
  Support = -> [BaseFeature005]
  sketch-geometry (4):
    g0: LineSegment StartX=2 StartY=-107.3 StartZ=0 EndX=8 EndY=-107.3 EndZ=0
    g1: LineSegment StartX=8 StartY=-107.3 StartZ=0 EndX=8 EndY=-101.3 EndZ=0
    g2: LineSegment StartX=8 StartY=-101.3 StartZ=0 EndX=2 EndY=-101.3 EndZ=0
    g3: LineSegment StartX=2 StartY=-101.3 StartZ=0 EndX=2 EndY=-107.3 EndZ=0
  constraints (10):
    c: Coincident(g0,g1)
    c: Coincident(g1,g2)
    c: Coincident(g2,g3)
    c: Coincident(g3,g0)
    c: Horizontal(g0)
    c: Horizontal(g2)
    c: Vertical(g1)
    c: Vertical(g3)
    c: DistanceX(g2,g2) = 6
    c: DistanceY(g1,g1) = 6
FEATURE [Part::Extrusion] Extrude015
  Base = -> Sketch023
  Dir = (0,0,1)
  DirMode = 2
  FaceMakerClass = Part::FaceMakerBullseye
  LengthFwd = 19.3
  LengthRev = 0
  Solid = true
  Symmetric = false
FEATURE [Sketcher::SketchObject] Sketch024
  FullyConstrained = false
  MapMode = 5
  Placement = pos=(0,0,21.3) rot=(0,0,1;0rad)
  Support = -> [Extrude015]
  sketch-geometry (1):
    g0: Circle CenterX=5 CenterY=-104.3 CenterZ=0 NormalX=0 NormalY=0 NormalZ=1 AngleXU=0 Radius=1.55
  constraints (1):
    c: Diameter(g0) = 3.1
FEATURE [PartDesign::Hole] Hole002  label="FRONT LEFT INSERT MNT"
  CustomThreadClearance = 0
  Depth = 2.5
  DepthType = 0
  Diameter = 3.2
  DrillForDepth = false
  DrillPoint = 1
  DrillPointAngle = 118
  HoleCutCountersinkAngle = 90
  HoleCutCustomValues = false
  HoleCutDepth = 0
  HoleCutDiameter = 6.1
  HoleCutType = 0
  ModelThread = false
  Profile = -> Sketch024
  Tapered = false
  TaperedAngle = 90
  ThreadClass = 0
  ThreadDepth = 2.5
  ThreadDepthType = 0
  ThreadDirection = 0
  ThreadFit = 0
  ThreadSize = 0
  ThreadType = 0
  Threaded = false
  UseCustomThreadClearance = false
FEATURE [Sketcher::SketchObject] Sketch025
  FullyConstrained = false
  MapMode = 5
  Placement = pos=(0,0,2) rot=(0,0,1;0rad)
  Support = -> [BaseFeature005]
  sketch-geometry (4):
    g0: LineSegment StartX=82.2 StartY=-107.3 StartZ=0 EndX=76.2 EndY=-107.3 EndZ=0
    g1: LineSegment StartX=76.2 StartY=-107.3 StartZ=0 EndX=76.2 EndY=-101.3 EndZ=0
    g2: LineSegment StartX=76.2 StartY=-101.3 StartZ=0 EndX=82.2 EndY=-101.3 EndZ=0
    g3: LineSegment StartX=82.2 StartY=-101.3 StartZ=0 EndX=82.2 EndY=-107.3 EndZ=0
  constraints (9):
    c: Coincident(g0,g1)
    c: Coincident(g1,g2)
    c: Coincident(g2,g3)
    c: Coincident(g3,g0)
    c: Horizontal(g0)
    c: Horizontal(g2)
    c: Vertical(g1)
    c: Vertical(g3)
    c: DistanceY(g1,g1) = 6
FEATURE [Part::Extrusion] Extrude016
  Base = -> Sketch025
  Dir = (0,0,1)
  DirMode = 2
  FaceMakerClass = Part::FaceMakerBullseye
  LengthFwd = 19.3
  LengthRev = 0
  Solid = true
  Symmetric = false
FEATURE [Sketcher::SketchObject] Sketch026
  FullyConstrained = false
  MapMode = 5
  Placement = pos=(0,0,21.3) rot=(0,0,1;0rad)
  Support = -> [Extrude016]
  sketch-geometry (1):
    g0: Circle CenterX=79.2 CenterY=-104.3 CenterZ=0 NormalX=0 NormalY=0 NormalZ=1 AngleXU=0 Radius=1.6
  constraints (1):
    c: Diameter(g0) = 3.2
FEATURE [PartDesign::Hole] Hole003  label="FRONT RIGHT INSERT MNT"
  CustomThreadClearance = 0
  Depth = 2.3
  DepthType = 0
  Diameter = 3.2
  DrillForDepth = false
  DrillPoint = 1
  DrillPointAngle = 118
  HoleCutCountersinkAngle = 90
  HoleCutCustomValues = false
  HoleCutDepth = 0
  HoleCutDiameter = 6.1
  HoleCutType = 0
  ModelThread = false
  Profile = -> Sketch026
  Tapered = false
  TaperedAngle = 90
  ThreadClass = 0
  ThreadDepth = 2.3
  ThreadDepthType = 0
  ThreadDirection = 0
  ThreadFit = 0
  ThreadSize = 0
  ThreadType = 0
  Threaded = false
  UseCustomThreadClearance = false
FEATURE [Sketcher::SketchObject] Sketch031
  FullyConstrained = false
  MapMode = 5
  Support = -> [XY_Plane012]
  sketch-geometry (4):
    g0: LineSegment StartX=0 StartY=-14.3705 StartZ=0 EndX=84.2 EndY=-14.3705 EndZ=0
    g1: LineSegment StartX=84.2 StartY=-14.3705 StartZ=0 EndX=84.2 EndY=-109.301 EndZ=0
    g2: LineSegment StartX=84.2 StartY=-109.301 StartZ=0 EndX=0 EndY=-109.301 EndZ=0
    g3: LineSegment StartX=0 StartY=-109.301 StartZ=0 EndX=0 EndY=-14.3705 EndZ=0
  constraints (11):
    c: Coincident(g0,g1)
    c: Coincident(g1,g2)
    c: Coincident(g2,g3)
    c: Coincident(g3,g0)
    c: Horizontal(g0)
    c: Horizontal(g2)
    c: Vertical(g1)
    c: Vertical(g3)
    c: PointOnObject(g0,g-2)
    c: DistanceX(g2,g2) = 84.2
    c: DistanceY(g1,g1) = 94.93
FEATURE [Part::Extrusion] Extrude019
  Base = -> Sketch031
  Dir = (0,0,1)
  DirMode = 2
  FaceMakerClass = Part::FaceMakerBullseye
  LengthFwd = 1.5
  LengthRev = 0
  Solid = true
  Symmetric = false
FEATURE [Sketcher::SketchObject] Sketch032
  FullyConstrained = false
  MapMode = 5
  Placement = pos=(0,0,1.5) rot=(0,0,1;0rad)
  Support = -> [Extrude019]
  sketch-geometry (4):
    g0: Circle CenterX=4 CenterY=-18.3995 CenterZ=0 NormalX=0 NormalY=0 NormalZ=1 AngleXU=0 Radius=1.6
    g1: Circle CenterX=80 CenterY=-18.4 CenterZ=0 NormalX=0 NormalY=0 NormalZ=1 AngleXU=0 Radius=1.6
    g2: Circle CenterX=79.2 CenterY=-104.3 CenterZ=0 NormalX=0 NormalY=0 NormalZ=1 AngleXU=0 Radius=1.6
    g3: Circle CenterX=5 CenterY=-104.3 CenterZ=0 NormalX=0 NormalY=0 NormalZ=1 AngleXU=0 Radius=1.6
  constraints (4):
    c: Diameter(g0) = 3.2
    c: Diameter(g1) = 3.2
    c: Diameter(g2) = 3.2
    c: Diameter(g3) = 3.2
FEATURE [PartDesign::Hole] Hole006  label="TOP PLATE WITH COUNTERSUNK HOLES"
  CustomThreadClearance = 0
  Depth = 2
  DepthType = 0
  Diameter = 2
  DrillForDepth = false
  DrillPoint = 0
  DrillPointAngle = 118
  HoleCutCountersinkAngle = 90
  HoleCutCustomValues = false
  HoleCutDepth = 2
  HoleCutDiameter = 3.8
  HoleCutType = 2
  ModelThread = false
  Profile = -> Sketch032
  Tapered = false
  TaperedAngle = 90
  ThreadClass = 0
  ThreadDepth = 2
  ThreadDepthType = 0
  ThreadDirection = 0
  ThreadFit = 0
  ThreadSize = 0
  ThreadType = 0
  Threaded = false
  UseCustomThreadClearance = false
FEATURE [Sketcher::SketchObject] Sketch034
  FullyConstrained = false
  MapMode = 5
  Placement = pos=(0,0,2) rot=(0,0,1;0rad)
  Support = -> [BaseFeature005]
  sketch-geometry (7):
    g0: LineSegment StartX=2 StartY=-99.8 StartZ=0 EndX=82.2 EndY=-99.8 EndZ=0
    g1: LineSegment StartX=2 StartY=-99.9 StartZ=0 EndX=42.1 EndY=-99.9 EndZ=0
    g2: LineSegment StartX=42.1 StartY=-100 StartZ=0 EndX=37.85 EndY=-100 EndZ=0
    g3: LineSegment StartX=37.85 StartY=-99.7927 StartZ=0 EndX=46.4 EndY=-99.7927 EndZ=0
    g4: LineSegment StartX=46.4 StartY=-99.7927 StartZ=0 EndX=46.4 EndY=-107.303 EndZ=0
    g5: LineSegment StartX=46.4 StartY=-107.303 StartZ=0 EndX=37.85 EndY=-107.303 EndZ=0
    g6: LineSegment StartX=37.85 StartY=-107.303 StartZ=0 EndX=37.85 EndY=-99.7927 EndZ=0
  constraints (15):
    c: Horizontal(g0)
    c: DistanceX(g0,g0) = 80.2
    c: Horizontal(g1)
    c: DistanceX(g1,g1) = 40.1
    c: Horizontal(g2)
    c: Coincident(g3,g4)
    c: Coincident(g4,g5)
    c: Coincident(g5,g6)
    c: Coincident(g6,g3)
    c: Horizontal(g3)
    c: Horizontal(g5)
    c: Vertical(g4)
    c: Vertical(g6)
    c: DistanceY(g4,g4) = 7.51
    c: DistanceX(g3,g3) = 8.55
FEATURE [Part::Extrusion] Extrude021
  Base = -> Sketch034
  Dir = (0,0,1)
  DirMode = 2
  FaceMakerClass = Part::FaceMakerBullseye
  LengthFwd = 5.5
  LengthRev = 0
  Solid = true
  Symmetric = false
FEATURE [Sketcher::SketchObject] Sketch036
  FullyConstrained = false
  MapMode = 5
  Placement = pos=(0,0,7.5) rot=(0,0,1;0rad)
  Support = -> [Extrude021]
  sketch-geometry (1):
    g0: Circle CenterX=42.15 CenterY=-103.5 CenterZ=0 NormalX=0 NormalY=0 NormalZ=1 AngleXU=0 Radius=2.25
  constraints (1):
    c: Diameter(g0) = 4.5
FEATURE [PartDesign::Hole] Hole007  label="FRONT LOCK SLOT"
  CustomThreadClearance = 0
  Depth = 5.5
  DepthType = 0
  Diameter = 4.5
  DrillForDepth = false
  DrillPoint = 0
  DrillPointAngle = 118
  HoleCutCountersinkAngle = 90
  HoleCutCustomValues = false
  HoleCutDepth = 0
  HoleCutDiameter = 6.1
  HoleCutType = 0
  ModelThread = false
  Profile = -> Sketch036
  Tapered = false
  TaperedAngle = 90
  ThreadClass = 0
  ThreadDepth = 5.5
  ThreadDepthType = 0
  ThreadDirection = 0
  ThreadFit = 0
  ThreadSize = 0
  ThreadType = 0
  Threaded = false
  UseCustomThreadClearance = false
FEATURE [Sketcher::SketchObject] Sketch037
  FullyConstrained = false
  MapMode = 5
  Placement = pos=(0,0,0) rot=(1,0,0;3.14159rad)
  Support = -> [Hole]
  sketch-geometry (1):
    g0: Circle CenterX=-134 CenterY=113.5 CenterZ=0 NormalX=0 NormalY=0 NormalZ=1 AngleXU=0 Radius=2.125
  constraints (1):
    c: Diameter(g0) = 4.25
FEATURE [Part::Extrusion] Extrude022  label="SPRING CYLINDER"
  Base = -> Sketch037
  Dir = (0,0,-1)
  DirMode = 2
  FaceMakerClass = Part::FaceMakerBullseye
  LengthFwd = 9
  LengthRev = 0
  Solid = true
  Symmetric = false
FEATURE [PartDesign::FeatureBase] BaseFeature
  BaseFeature = -> Extrude005
FEATURE [Sketcher::SketchObject] Sketch009
  FullyConstrained = false
  MapMode = 5
  Placement = pos=(0,-14.4,0) rot=(0,0.707107,0.707107;3.14159rad)
  Support = -> [BaseFeature]
  sketch-geometry (4):
    g0: LineSegment StartX=-7 StartY=10 StartZ=0 EndX=-24.64 EndY=10 EndZ=0
    g1: LineSegment StartX=-24.64 StartY=10 StartZ=0 EndX=-24.64 EndY=14 EndZ=0
    g2: LineSegment StartX=-24.64 StartY=14 StartZ=0 EndX=-7 EndY=14 EndZ=0
    g3: LineSegment StartX=-7 StartY=14 StartZ=0 EndX=-7 EndY=10 EndZ=0
  constraints (10):
    c: Coincident(g0,g1)
    c: Coincident(g1,g2)
    c: Coincident(g2,g3)
    c: Coincident(g3,g0)
    c: Horizontal(g0)
    c: Horizontal(g2)
    c: Vertical(g1)
    c: Vertical(g3)
    c: DistanceX(g2,g2) = 17.64
    c: DistanceY(g1,g1) = 4
FEATURE [PartDesign::Pocket] Pocket  label="BACK WALL"
  Direction = (0,-1,2e-16)
  Length = 2
  Length2 = 5
  Profile = -> Sketch009
  ReferenceAxis = -> Sketch009 [N_Axis]
  Type = 0
FEATURE [Sketcher::SketchObject] Sketch027
  FullyConstrained = false
  MapMode = 5
  Placement = pos=(0,-16.37,0) rot=(1,0,0;1.5708rad)
  Support = -> [Pocket]
  sketch-geometry (4):
    g0: LineSegment StartX=2 StartY=21.3 StartZ=0 EndX=7 EndY=21.3 EndZ=0
    g1: LineSegment StartX=7 StartY=21.3 StartZ=0 EndX=7 EndY=16.3 EndZ=0
    g2: LineSegment StartX=7 StartY=16.3 StartZ=0 EndX=2 EndY=16.3 EndZ=0
    g3: LineSegment StartX=2 StartY=16.3 StartZ=0 EndX=2 EndY=21.3 EndZ=0
  constraints (10):
    c: Coincident(g0,g1)
    c: Coincident(g1,g2)
    c: Coincident(g2,g3)
    c: Coincident(g3,g0)
    c: Horizontal(g0)
    c: Horizontal(g2)
    c: Vertical(g1)
    c: Vertical(g3)
    c: DistanceY(g1,g1) = 5
    c: DistanceX(g0,g0) = 5
FEATURE [Sketcher::SketchObject] Sketch029
  FullyConstrained = false
  MapMode = 5
  Placement = pos=(0,-16.37,0) rot=(1,0,0;1.5708rad)
  Support = -> [Pocket]
  sketch-geometry (4):
    g0: LineSegment StartX=82.2 StartY=21.3 StartZ=0 EndX=77.2 EndY=21.3 EndZ=0
    g1: LineSegment StartX=77.2 StartY=21.3 StartZ=0 EndX=77.2 EndY=16.3 EndZ=0
    g2: LineSegment StartX=77.2 StartY=16.3 StartZ=0 EndX=82.2 EndY=16.3 EndZ=0
    g3: LineSegment StartX=82.2 StartY=16.3 StartZ=0 EndX=82.2 EndY=21.3 EndZ=0
  constraints (10):
    c: Coincident(g0,g1)
    c: Coincident(g1,g2)
    c: Coincident(g2,g3)
    c: Coincident(g3,g0)
    c: Horizontal(g0)
    c: Horizontal(g2)
    c: Vertical(g1)
    c: Vertical(g3)
    c: DistanceX(g0,g0) = 5
    c: DistanceY(g3,g3) = 5
FEATURE [Part::Extrusion] Extrude018
  Base = -> Sketch029
  Dir = (0,-1,2e-16)
  DirMode = 2
  FaceMakerClass = Part::FaceMakerBullseye
  LengthFwd = 5
  LengthRev = 0
  Solid = true
  Symmetric = false
FEATURE [Sketcher::SketchObject] Sketch030
  FullyConstrained = false
  MapMode = 5
  Placement = pos=(0,4.7e-15,21.3) rot=(0,0,1;0rad)
  Support = -> [Extrude018]
  sketch-geometry (1):
    g0: Circle CenterX=80 CenterY=-18.4 CenterZ=0 NormalX=0 NormalY=0 NormalZ=1 AngleXU=0 Radius=1.6
  constraints (1):
    c: Diameter(g0) = 3.2
FEATURE [PartDesign::Hole] Hole005  label="BACK RIGHT INSERT MNT"
  CustomThreadClearance = 0
  Depth = 2.3
  DepthType = 0
  Diameter = 3.2
  DrillForDepth = false
  DrillPoint = 1
  DrillPointAngle = 118
  HoleCutCountersinkAngle = 90
  HoleCutCustomValues = false
  HoleCutDepth = 0
  HoleCutDiameter = 6.1
  HoleCutType = 0
  ModelThread = false
  Profile = -> Sketch030
  Tapered = false
  TaperedAngle = 90
  ThreadClass = 0
  ThreadDepth = 2.3
  ThreadDepthType = 0
  ThreadDirection = 0
  ThreadFit = 0
  ThreadSize = 0
  ThreadType = 0
  Threaded = false
  UseCustomThreadClearance = false
FEATURE [Part::Extrusion] Extrude017
  Base = -> Sketch027
  Dir = (0,-1,2e-16)
  DirMode = 2
  FaceMakerClass = Part::FaceMakerBullseye
  LengthFwd = 5
  LengthRev = 0
  Solid = true
  Symmetric = false
FEATURE [Sketcher::SketchObject] Sketch028
  FullyConstrained = false
  MapMode = 5
  Placement = pos=(0,4.7e-15,21.3) rot=(0,0,1;0rad)
  Support = -> [Extrude017]
  sketch-geometry (1):
    g0: Circle CenterX=4 CenterY=-18.4 CenterZ=0 NormalX=0 NormalY=0 NormalZ=1 AngleXU=0 Radius=1.6
  constraints (1):
    c: Diameter(g0) = 3.2
FEATURE [PartDesign::Hole] Hole004  label="BACK LEFT INSERT MNT"
  CustomThreadClearance = 0
  Depth = 2.2
  DepthType = 0
  Diameter = 3.2
  DrillForDepth = false
  DrillPoint = 1
  DrillPointAngle = 118
  HoleCutCountersinkAngle = 90
  HoleCutCustomValues = false
  HoleCutDepth = 0
  HoleCutDiameter = 6.1
  HoleCutType = 0
  ModelThread = false
  Profile = -> Sketch028
  Tapered = false
  TaperedAngle = 90
  ThreadClass = 0
  ThreadDepth = 2.2
  ThreadDepthType = 0
  ThreadDirection = 0
  ThreadFit = 0
  ThreadSize = 0
  ThreadType = 0
  Threaded = false
  UseCustomThreadClearance = false
FEATURE [Sketcher::SketchObject] Sketch038
  FullyConstrained = false
  MapMode = 5
  Placement = pos=(0,0,1.5) rot=(0,0,1;0rad)
  Support = -> [Hole006]
  sketch-geometry (4):
    g0: LineSegment StartX=36.86 StartY=-100.71 StartZ=0 EndX=47.46 EndY=-100.71 EndZ=0
    g1: LineSegment StartX=47.46 StartY=-100.71 StartZ=0 EndX=47.46 EndY=-106.31 EndZ=0
    g2: LineSegment StartX=47.46 StartY=-106.31 StartZ=0 EndX=36.86 EndY=-106.31 EndZ=0
    g3: LineSegment StartX=36.86 StartY=-106.31 StartZ=0 EndX=36.86 EndY=-100.71 EndZ=0
  constraints (10):
    c: Coincident(g0,g1)
    c: Coincident(g1,g2)
    c: Coincident(g2,g3)
    c: Coincident(g3,g0)
    c: Horizontal(g0)
    c: Horizontal(g2)
    c: Vertical(g1)
    c: Vertical(g3)
    c: DistanceX(g0,g0) = 10.6
    c: DistanceY(g3,g3) = 5.6
FEATURE [Sketcher::SketchObject] Sketch039
  FullyConstrained = false
  MapMode = 5
  Placement = pos=(0,0,7) rot=(0,0,1;0rad)
  Support = -> [Hole]
  sketch-geometry (4):
    g0: LineSegment StartX=-139 StartY=-111 StartZ=0 EndX=-129 EndY=-111 EndZ=0
    g1: LineSegment StartX=-129 StartY=-111 StartZ=0 EndX=-129 EndY=-116 EndZ=0
    g2: LineSegment StartX=-129 StartY=-116 StartZ=0 EndX=-139 EndY=-116 EndZ=0
    g3: LineSegment StartX=-139 StartY=-116 StartZ=0 EndX=-139 EndY=-111 EndZ=0
  constraints (10):
    c: Coincident(g0,g1)
    c: Coincident(g1,g2)
    c: Coincident(g2,g3)
    c: Coincident(g3,g0)
    c: Horizontal(g0)
    c: Horizontal(g2)
    c: Vertical(g1)
    c: Vertical(g3)
    c: DistanceY(g1,g1) = 5
    c: DistanceX(g0,g0) = 10
FEATURE [Part::Extrusion] Extrude023
  Base = -> Sketch039
  Dir = (0,0,1)
  DirMode = 2
  FaceMakerClass = Part::FaceMakerBullseye
  LengthFwd = 4.5
  LengthRev = 0
  Solid = true
  Symmetric = false
FEATURE [Sketcher::SketchObject] Sketch040
  FullyConstrained = false
  MapMode = 5
  Placement = pos=(-129,0,0) rot=(0.57735,0.57735,0.57735;2.0944rad)
  Support = -> [Extrude023]
  sketch-geometry (3):
    g0: LineSegment StartX=-110.99 StartY=8.49 StartZ=0 EndX=-116 EndY=11.5 EndZ=0
    g1: LineSegment StartX=-116 StartY=11.5 StartZ=0 EndX=-110.99 EndY=11.5 EndZ=0
    g2: LineSegment StartX=-110.99 StartY=11.5 StartZ=0 EndX=-110.99 EndY=8.49 EndZ=0
  constraints (7):
    c: Coincident(g0,g1)
    c: Horizontal(g1)
    c: Coincident(g1,g2)
    c: Coincident(g2,g0)
    c: Vertical(g2)
    c: DistanceY(g2,g2) = 3.01
    c: DistanceX(g1,g1) = 5.01
FEATURE [PartDesign::FeatureBase] BaseFeature006
  BaseFeature = -> Extrude023
FEATURE [PartDesign::Pocket] Pocket004  label="LOCK SLIDE HOOK"
  Direction = (-1,0,0)
  Length = 10
  Length2 = 5
  Profile = -> Sketch040
  ReferenceAxis = -> Sketch040 [N_Axis]
  Type = 0
FEATURE [Sketcher::SketchObject] Sketch041
  FullyConstrained = true
  MapMode = 5
  Support = -> [XY_Plane005]
FEATURE [PartDesign::Body] Body002  label="LOCK MECHANISM BODY"
  Group = -> [Sketch041]
  Origin = -> Origin005
FEATURE [App::Part] Part002  label="locking mechanism"
  Group = -> [Body002,BaseFeature002,BaseFeature003,Sketch016,Extrude007,Sketch040,Sketch015,Sketch012,BaseFeature006,Pocket002,Sketch011,Sketch037,Sketch039,Extrude022,Extrude023,Pocket004,Hole]
  Origin = -> Origin004
  Placement = pos=(176.16,9.99,14.45) rot=(0,0,1;0rad)
FEATURE [PartDesign::Pocket] Pocket005  label="TOP PLATE WITH LOCK POCKET"
  BaseFeature = -> Hole006
  Direction = (0,0,-1)
  Length = 1.5
  Length2 = 5
  Profile = -> Sketch038
  ReferenceAxis = -> Sketch038 [N_Axis]
  Type = 0
FEATURE [PartDesign::Body] Body006  label="TOP PLATE BODY"
  Group = -> [Sketch032,Hole006,Sketch038,Pocket005]
  Origin = -> Origin012
  Tip = -> Pocket005
FEATURE [App::Part] Part005  label="top plate"
  Group = -> [Body006,Sketch031,Extrude019]
  Origin = -> Origin011
  Placement = pos=(0,0,21.28) rot=(0,0,1;0rad)
FEATURE [Sketcher::SketchObject] Sketch042
  FullyConstrained = false
  MapMode = 5
  Placement = pos=(0,-109.3,0) rot=(1,0,0;1.5708rad)
  Support = -> [Extrude014]
  sketch-geometry (4):
    g0: LineSegment StartX=40.86 StartY=19.75 StartZ=0 EndX=43.5 EndY=19.75 EndZ=0
    g1: LineSegment StartX=43.5 StartY=19.75 StartZ=0 EndX=43.5 EndY=12.6 EndZ=0
    g2: LineSegment StartX=43.5 StartY=12.6 StartZ=0 EndX=40.86 EndY=12.6 EndZ=0
    g3: LineSegment StartX=40.86 StartY=12.6 StartZ=0 EndX=40.86 EndY=19.75 EndZ=0
  constraints (10):
    c: Coincident(g0,g1)
    c: Coincident(g1,g2)
    c: Coincident(g2,g3)
    c: Coincident(g3,g0)
    c: Horizontal(g0)
    c: Horizontal(g2)
    c: Vertical(g1)
    c: Vertical(g3)
    c: DistanceX(g0,g0) = 2.64
    c: DistanceY(g3,g3) = 7.15
FEATURE [Part::Extrusion] Extrude024
  Base = -> Sketch017
  Dir = (1,-1e-16,1e-16)
  DirMode = 2
  FaceMakerClass = Part::FaceMakerBullseye
  LengthFwd = 2
  LengthRev = 0
  Solid = true
  Symmetric = false
FEATURE [Sketcher::SketchObject] Sketch043
  FullyConstrained = false
  MapMode = 5
  Placement = pos=(2,-4e-16,4e-16) rot=(0.57735,0.57735,0.57735;2.0944rad)
  Support = -> [Extrude024]
  sketch-geometry (1):
    g0: Circle CenterX=-125.95 CenterY=3.5 CenterZ=0 NormalX=0 NormalY=0 NormalZ=1 AngleXU=0 Radius=0.75
  constraints (1):
    c: Diameter(g0) = 1.5
FEATURE [PartDesign::Hole] Hole008  label="BASE HANDLE INSERT"
  CustomThreadClearance = 0
  Depth = 2
  DepthType = 0
  Diameter = 1.5
  DrillForDepth = false
  DrillPoint = 1
  DrillPointAngle = 118
  HoleCutCountersinkAngle = 90
  HoleCutCustomValues = false
  HoleCutDepth = 0
  HoleCutDiameter = 6.1
  HoleCutType = 0
  ModelThread = false
  Profile = -> Sketch043
  Tapered = false
  TaperedAngle = 90
  ThreadClass = 0
  ThreadDepth = 2
  ThreadDepthType = 0
  ThreadDirection = 0
  ThreadFit = 0
  ThreadSize = 0
  ThreadType = 0
  Threaded = false
  UseCustomThreadClearance = false
FEATURE [PartDesign::FeatureBase] BaseFeature007
  BaseFeature = -> Extrude014
FEATURE [PartDesign::Pocket] Pocket006  label="FRONT WALL WITH HANDLE SLOT"
  BaseFeature = -> BaseFeature007
  Direction = (0,1,-2e-16)
  Length = 2
  Length2 = 5
  Profile = -> Sketch042
  ReferenceAxis = -> Sketch042 [N_Axis]
  Type = 0
FEATURE [App::MeasureDistance] Distance  label="Distance: 3.33780 mm"
  Distance = 3.3378
  P1 = (43.5,-109.3,19.3861)
  P2 = (43.16,-112.62,19.44)
FEATURE [App::MeasureDistance] Distance001  label="Distance: 94.93000 mm"
  Distance = 94.93
  P1 = (84.2,-109.301,22.88)
  P2 = (84.2,-14.3705,22.88)
FEATURE [App::MeasureDistance] Distance002  label="Distance: 84.03434 mm"
  Distance = 84.0343
  P1 = (0.165655,-109.301,22.88)
  P2 = (84.2,-109.301,22.88)
FEATURE [App::MeasureDistance] Distance003  label="Distance: 22.78329 mm"
  Distance = 22.7833
  P1 = (0,-14.3705,22.7833)
  P2 = (0,-14.4,0)
FEATURE [App::MeasureDistance] Distance004  label="Distance: 10.06841 mm"
  Distance = 10.0684
  P1 = (82.0192,-16.37,21.3)
  P2 = (82.2,-26.4368,21.3)
FEATURE [App::MeasureDistance] Distance005  label="Distance: 7.48747 mm"
  Distance = 7.48747
  P1 = (82.0952,-107.281,21.3)
  P2 = (82.1396,-99.794,21.3)
FEATURE [App::MeasureDistance] Distance007  label="Distance: 1.03116 mm"
  Distance = 1.03116
  P1 = (82.2,-95.6714,11.6529)
  P2 = (82.1272,-96.7,11.65)
FEATURE [App::MeasureDistance] Distance008  label="Distance: 0.98878 mm"
  Distance = 0.988782
  P1 = (62.8884,-97.788,21.3)
  P2 = (61.9,-97.7591,21.3)
FEATURE [Sketcher::SketchObject] Sketch044
  FullyConstrained = false
  MapMode = 5
  Placement = pos=(0,-28.49,0) rot=(1,0,0;1.5708rad)
  Support = -> [Extrude001]
  sketch-geometry (8):
    g0: ArcOfCircle CenterX=11.5 CenterY=21.374 CenterZ=0 NormalX=0 NormalY=0 NormalZ=1 AngleXU=0 Radius=7.50005 StartAngle=3.13813 EndAngle=6.28665
    g1: LineSegment StartX=4 StartY=21.4 StartZ=0 EndX=19 EndY=21.4 EndZ=0
    g2: ArcOfCircle CenterX=32 CenterY=21.3845 CenterZ=0 NormalX=0 NormalY=0 NormalZ=1 AngleXU=0 Radius=8.00001 StartAngle=3.13966 EndAngle=6.28512
    g3: LineSegment StartX=24 StartY=21.4 StartZ=0 EndX=40 EndY=21.4 EndZ=0
    g4: ArcOfCircle CenterX=52.2 CenterY=21.3636 CenterZ=0 NormalX=0 NormalY=0 NormalZ=1 AngleXU=0 Radius=7.80009 StartAngle=3.13692 EndAngle=6.28785
    g5: LineSegment StartX=60 StartY=21.4 StartZ=0 EndX=44.4 EndY=21.4 EndZ=0
    g6: ArcOfCircle CenterX=72.5 CenterY=21.2875 CenterZ=0 NormalX=0 NormalY=0 NormalZ=1 AngleXU=0 Radius=7.50084 StartAngle=3.12659 EndAngle=6.29819
    g7: LineSegment StartX=80 StartY=21.4 StartZ=0 EndX=65 EndY=21.4 EndZ=0
  constraints (19):
    c: Coincident(g1,g0)
    c: Coincident(g1,g0)
    c: Horizontal(g1)
    c: DistanceX(g1,g1) = 15
    c: Diameter(g0) = 15.0001
    c: Coincident(g3,g2)
    c: Coincident(g3,g2)
    c: Horizontal(g3)
    c: DistanceX(g3,g3) = 16
    c: Diameter(g2) = 16
    c: Coincident(g5,g4)
    c: Coincident(g5,g4)
    c: Horizontal(g5)
    c: DistanceX(g5,g5) = 15.6
    c: Diameter(g4) = 15.6002
    c: Coincident(g7,g6)
    c: Coincident(g7,g6)
    c: Horizontal(g7)
    c: DistanceX(g7,g7) = 15
FEATURE [PartDesign::FeatureBase] BaseFeature008
  BaseFeature = -> Extrude001
FEATURE [PartDesign::Pocket] Pocket007  label="cell walls"
  BaseFeature = -> BaseFeature008
  Direction = (0,1,-2e-16)
  Length = 5
  Length2 = 5
  Profile = -> Sketch044
  ReferenceAxis = -> Sketch044 [N_Axis]
  Type = 0
FEATURE [Sketcher::SketchObject] Sketch046
  FullyConstrained = false
  MapMode = 5
  Placement = pos=(2,-4e-16,4e-16) rot=(0.57735,0.57735,0.57735;2.0944rad)
  Support = -> [Hole008]
  sketch-geometry (9):
    g0: LineSegment StartX=-133.3 StartY=5 StartZ=0 EndX=-133.3 EndY=3 EndZ=0
    g1: LineSegment StartX=-133.3 StartY=3 StartZ=0 EndX=-131.8 EndY=3 EndZ=0
    g2: LineSegment StartX=-131.8 StartY=3 StartZ=0 EndX=-131.8 EndY=-7 EndZ=0
    g3: LineSegment StartX=-131.8 StartY=-7 StartZ=0 EndX=-133.3 EndY=-7 EndZ=0
    g4: LineSegment StartX=-133.3 StartY=-7 StartZ=0 EndX=-133.3 EndY=-9 EndZ=0
    g5: LineSegment StartX=-133.3 StartY=-9 StartZ=0 EndX=-130.3 EndY=-9 EndZ=0
    g6: LineSegment StartX=-130.3 StartY=-9 StartZ=0 EndX=-130.3 EndY=2 EndZ=0
    g7: LineSegment StartX=-130.3 StartY=2 StartZ=0 EndX=-130.3 EndY=5 EndZ=0
    g8: LineSegment StartX=-130.3 StartY=5 StartZ=0 EndX=-133.3 EndY=5 EndZ=0
  constraints (25):
    c: Vertical(g0)
    c: Coincident(g0,g1)
    c: Horizontal(g1)
    c: Coincident(g1,g2)
    c: Vertical(g2)
    c: Coincident(g2,g3)
    c: Horizontal(g3)
    c: Coincident(g3,g4)
    c: Vertical(g4)
    c: Coincident(g4,g5)
    c: Horizontal(g5)
    c: Coincident(g5,g6)
    c: Vertical(g6)
    c: Coincident(g6,g7)
    c: Vertical(g7)
    c: Coincident(g7,g8)
    c: Coincident(g8,g0)
    c: Horizontal(g8)
    c: DistanceX(g8,g8) = 3
    c: DistanceX(g1,g1) = 1.5
    c: DistanceX(g3,g3) = 1.50001
    c: DistanceY(g6,g6) = 11
    c: DistanceY(g2,g2) = 10
    c: DistanceY(g4,g4) = 2
    c: DistanceY(g0,g0) = 2
FEATURE [Part::Extrusion] Extrude025
  Base = -> Sketch046
  Dir = (1,-2e-16,2e-16)
  DirMode = 2
  FaceMakerClass = Part::FaceMakerBullseye
  LengthFwd = 10
  LengthRev = 0
  Solid = true
  Symmetric = false
FEATURE [Sketcher::SketchObject] Sketch047
  FullyConstrained = false
  MapMode = 5
  Placement = pos=(-3e-16,0,0) rot=(-0.57735,0.57735,0.57735;4.18879rad)
  Support = -> [Hole008]
  sketch-geometry (9):
    g0: LineSegment StartX=133.3 StartY=5 StartZ=0 EndX=133.3 EndY=3 EndZ=0
    g1: LineSegment StartX=133.3 StartY=3 StartZ=0 EndX=131.8 EndY=3 EndZ=0
    g2: LineSegment StartX=131.8 StartY=3 StartZ=0 EndX=131.8 EndY=-7 EndZ=0
    g3: LineSegment StartX=131.8 StartY=-7 StartZ=0 EndX=133.3 EndY=-7 EndZ=0
    g4: LineSegment StartX=133.3 StartY=-7 StartZ=0 EndX=133.3 EndY=-9 EndZ=0
    g5: LineSegment StartX=133.3 StartY=-9 StartZ=0 EndX=130.3 EndY=-9 EndZ=0
    g6: LineSegment StartX=130.3 StartY=-9 StartZ=0 EndX=130.3 EndY=2 EndZ=0
    g7: LineSegment StartX=130.3 StartY=2 StartZ=0 EndX=130.3 EndY=5 EndZ=0
    g8: LineSegment StartX=130.3 StartY=5 StartZ=0 EndX=133.3 EndY=5 EndZ=0
  constraints (25):
    c: Vertical(g0)
    c: Coincident(g0,g1)
    c: Horizontal(g1)
    c: Coincident(g1,g2)
    c: Vertical(g2)
    c: Coincident(g2,g3)
    c: Horizontal(g3)
    c: Coincident(g3,g4)
    c: Vertical(g4)
    c: Coincident(g4,g5)
    c: Horizontal(g5)
    c: Coincident(g5,g6)
    c: Vertical(g6)
    c: Coincident(g6,g7)
    c: Vertical(g7)
    c: Coincident(g7,g8)
    c: Coincident(g8,g0)
    c: Horizontal(g8)
    c: DistanceX(g8,g8) = 3
    c: DistanceX(g1,g1) = 1.49999
    c: DistanceX(g5,g5) = 3
    c: DistanceY(g6,g6) = 11
    c: DistanceY(g4,g4) = 2
    c: DistanceY(g2,g2) = 10
    c: DistanceY(g0,g0) = 2
FEATURE [Part::Extrusion] Extrude026
  Base = -> Sketch047
  Dir = (-1,2e-16,-2e-16)
  DirMode = 2
  FaceMakerClass = Part::FaceMakerBullseye
  LengthFwd = 10
  LengthRev = 0
  Solid = true
  Symmetric = false
FEATURE [App::Part] Part003  label="locking handle"
  Group = -> [Extrude024,Sketch017,Body003,Hole008,Sketch043,Sketch046,Extrude025,Sketch047,Extrude026]
  Origin = -> Origin006
  Placement = pos=(41.16,20.68,14.44) rot=(0,0,1;0rad)
FEATURE [App::Part] Part007  label="Locking Components"
  Group = -> [Part002,Part003,Part004]
  Origin = -> Origin014
FEATURE [Sketcher::SketchObject] Sketch048
  FullyConstrained = false
  MapMode = 5
  Placement = pos=(0,-109.3,0) rot=(1,0,0;1.5708rad)
  Support = -> [Pocket006]
  sketch-geometry (32):
    g0: Circle CenterX=10 CenterY=16 CenterZ=0 NormalX=0 NormalY=0 NormalZ=1 AngleXU=0 Radius=0.5
    g1: Circle CenterX=11.3 CenterY=16 CenterZ=0 NormalX=0 NormalY=0 NormalZ=1 AngleXU=0 Radius=0.5
    g2: Circle CenterX=10 CenterY=14.7 CenterZ=0 NormalX=0 NormalY=0 NormalZ=1 AngleXU=0 Radius=0.5
    g3: Circle CenterX=11.3 CenterY=14.7 CenterZ=0 NormalX=0 NormalY=0 NormalZ=1 AngleXU=0 Radius=0.5
    g4: Circle CenterX=12.6 CenterY=14.7 CenterZ=0 NormalX=0 NormalY=0 NormalZ=1 AngleXU=0 Radius=0.5
    g5: Circle CenterX=13.9 CenterY=14.7 CenterZ=0 NormalX=0 NormalY=0 NormalZ=1 AngleXU=0 Radius=0.5
    g6: Circle CenterX=15.2 CenterY=14.7 CenterZ=0 NormalX=0 NormalY=0 NormalZ=1 AngleXU=0 Radius=0.5
    g7: Circle CenterX=12.6 CenterY=16 CenterZ=0 NormalX=0 NormalY=0 NormalZ=1 AngleXU=0 Radius=0.5
    g8: Circle CenterX=13.9 CenterY=16 CenterZ=0 NormalX=0 NormalY=0 NormalZ=1 AngleXU=0 Radius=0.5
    g9: Circle CenterX=15.2 CenterY=16 CenterZ=0 NormalX=0 NormalY=0 NormalZ=1 AngleXU=0 Radius=0.5
    g10: Circle CenterX=10 CenterY=13.4 CenterZ=0 NormalX=0 NormalY=0 NormalZ=1 AngleXU=0 Radius=0.5
    g11: Circle CenterX=11.3 CenterY=13.4 CenterZ=0 NormalX=0 NormalY=0 NormalZ=1 AngleXU=0 Radius=0.5
    g12: Circle CenterX=12.6 CenterY=13.4 CenterZ=0 NormalX=0 NormalY=0 NormalZ=1 AngleXU=0 Radius=0.5
    g13: Circle CenterX=13.9 CenterY=13.4 CenterZ=0 NormalX=0 NormalY=0 NormalZ=1 AngleXU=0 Radius=0.5
    g14: Circle CenterX=15.2 CenterY=13.4 CenterZ=0 NormalX=0 NormalY=0 NormalZ=1 AngleXU=0 Radius=0.5
    g15: Circle CenterX=10 CenterY=12.1 CenterZ=0 NormalX=0 NormalY=0 NormalZ=1 AngleXU=0 Radius=0.5
    g16: Circle CenterX=11.3 CenterY=12.1 CenterZ=0 NormalX=0 NormalY=0 NormalZ=1 AngleXU=0 Radius=0.5
    g17: Circle CenterX=12.6 CenterY=12.1 CenterZ=0 NormalX=0 NormalY=0 NormalZ=1 AngleXU=0 Radius=0.5
    g18: Circle CenterX=13.9 CenterY=12.1 CenterZ=0 NormalX=0 NormalY=0 NormalZ=1 AngleXU=0 Radius=0.5
    g19: Circle CenterX=15.2 CenterY=12.1 CenterZ=0 NormalX=0 NormalY=0 NormalZ=1 AngleXU=0 Radius=0.5
    g20: Circle CenterX=16.5 CenterY=16 CenterZ=0 NormalX=0 NormalY=0 NormalZ=1 AngleXU=0 Radius=0.5
    g21: Circle CenterX=16.5 CenterY=14.7 CenterZ=0 NormalX=0 NormalY=0 NormalZ=1 AngleXU=0 Radius=0.5
    g22: Circle CenterX=16.5 CenterY=13.4 CenterZ=0 NormalX=0 NormalY=0 NormalZ=1 AngleXU=0 Radius=0.5
    g23: Circle CenterX=16.5 CenterY=12.1 CenterZ=0 NormalX=0 NormalY=0 NormalZ=1 AngleXU=0 Radius=0.5
    g24: Circle CenterX=17.8 CenterY=16 CenterZ=0 NormalX=0 NormalY=0 NormalZ=1 AngleXU=0 Radius=0.5
    g25: Circle CenterX=19.1 CenterY=16 CenterZ=0 NormalX=0 NormalY=0 NormalZ=1 AngleXU=0 Radius=0.5
    g26: Circle CenterX=17.8 CenterY=14.7 CenterZ=0 NormalX=0 NormalY=0 NormalZ=1 AngleXU=0 Radius=0.5
    g27: Circle CenterX=19.1 CenterY=14.7 CenterZ=0 NormalX=0 NormalY=0 NormalZ=1 AngleXU=0 Radius=0.5
    g28: Circle CenterX=17.8 CenterY=13.4 CenterZ=0 NormalX=0 NormalY=0 NormalZ=1 AngleXU=0 Radius=0.5
    g29: Circle CenterX=19.1 CenterY=13.4 CenterZ=0 NormalX=0 NormalY=0 NormalZ=1 AngleXU=0 Radius=0.5
    g30: Circle CenterX=17.8 CenterY=12.1 CenterZ=0 NormalX=0 NormalY=0 NormalZ=1 AngleXU=0 Radius=0.5
    g31: Circle CenterX=19.1 CenterY=12.1 CenterZ=0 NormalX=0 NormalY=0 NormalZ=1 AngleXU=0 Radius=0.5
  constraints (32):
    c: Diameter(g0) = 1
    c: Diameter(g1) = 1
    c: Diameter(g7) = 1
    c: Diameter(g8) = 1
    c: Diameter(g9) = 1
    c: Diameter(g2) = 1
    c: Diameter(g3) = 1
    c: Diameter(g4) = 1
    c: Diameter(g5) = 1
    c: Diameter(g6) = 1
    c: Diameter(g10) = 1
    c: Diameter(g11) = 1
    c: Diameter(g12) = 1
    c: Diameter(g13) = 1
    c: Diameter(g14) = 1
    c: Diameter(g19) = 1
    c: Diameter(g18) = 1
    c: Diameter(g17) = 1
    c: Diameter(g16) = 1
    c: Diameter(g15) = 1
    c: Diameter(g20) = 1
    c: Diameter(g21) = 1
    c: Diameter(g22) = 1
    c: Diameter(g23) = 1
    c: Diameter(g24) = 1
    c: Diameter(g26) = 1
    c: Diameter(g28) = 1
    c: Diameter(g30) = 1
    c: Diameter(g31) = 1
    c: Diameter(g29) = 1
    c: Diameter(g27) = 1
    c: Diameter(g25) = 1
FEATURE [PartDesign::Hole] Hole009
  CustomThreadClearance = 0
  Depth = 2
  DepthType = 0
  Diameter = 1
  DrillForDepth = false
  DrillPoint = 0
  DrillPointAngle = 118
  HoleCutCountersinkAngle = 90
  HoleCutCustomValues = false
  HoleCutDepth = 0
  HoleCutDiameter = 6.1
  HoleCutType = 0
  ModelThread = false
  Profile = -> Sketch048
  Tapered = false
  TaperedAngle = 90
  ThreadClass = 0
  ThreadDepth = 2
  ThreadDepthType = 0
  ThreadDirection = 0
  ThreadFit = 0
  ThreadSize = 0
  ThreadType = 0
  Threaded = false
  UseCustomThreadClearance = false
FEATURE [PartDesign::Body] Body005  label="FRONT BODY"
  Group = -> [Sketch048,Hole009]
  Origin = -> Origin010
  Tip = -> Hole009
FEATURE [Sketcher::SketchObject] Sketch049
  FullyConstrained = false
  MapMode = 5
  Placement = pos=(0,-99.794,0) rot=(1,0,0;1.5708rad)
  Support = -> [Pocket007]
  sketch-geometry (8):
    g0: ArcOfCircle CenterX=11.5 CenterY=21.374 CenterZ=0 NormalX=0 NormalY=0 NormalZ=1 AngleXU=0 Radius=7.50005 StartAngle=3.13813 EndAngle=6.28665
    g1: LineSegment StartX=4 StartY=21.4 StartZ=0 EndX=19 EndY=21.4 EndZ=0
    g2: ArcOfCircle CenterX=32 CenterY=21.3845 CenterZ=0 NormalX=0 NormalY=0 NormalZ=1 AngleXU=0 Radius=8.00001 StartAngle=3.13966 EndAngle=6.28512
    g3: LineSegment StartX=24 StartY=21.4 StartZ=0 EndX=40 EndY=21.4 EndZ=0
    g4: ArcOfCircle CenterX=52.2 CenterY=21.3636 CenterZ=0 NormalX=0 NormalY=0 NormalZ=1 AngleXU=0 Radius=7.80009 StartAngle=3.13692 EndAngle=6.28785
    g5: LineSegment StartX=60 StartY=21.4 StartZ=0 EndX=44.4 EndY=21.4 EndZ=0
    g6: ArcOfCircle CenterX=72.5 CenterY=21.2875 CenterZ=0 NormalX=0 NormalY=0 NormalZ=1 AngleXU=0 Radius=7.50084 StartAngle=3.12659 EndAngle=6.29819
    g7: LineSegment StartX=80 StartY=21.4 StartZ=0 EndX=65 EndY=21.4 EndZ=0
  constraints (19):
    c: Coincident(g1,g0)
    c: Coincident(g1,g0)
    c: Horizontal(g1)
    c: DistanceX(g1,g1) = 15
    c: Diameter(g0) = 15.0001
    c: Coincident(g3,g2)
    c: Coincident(g3,g2)
    c: Horizontal(g3)
    c: DistanceX(g3,g3) = 16
    c: Diameter(g2) = 16
    c: Coincident(g5,g4)
    c: Coincident(g5,g4)
    c: Horizontal(g5)
    c: DistanceX(g5,g5) = 15.6
    c: Diameter(g4) = 15.6002
    c: Coincident(g7,g6)
    c: Coincident(g7,g6)
    c: Horizontal(g7)
    c: DistanceX(g7,g7) = 15
FEATURE [PartDesign::FeatureBase] BaseFeature009
  BaseFeature = -> Pocket007
FEATURE [PartDesign::Pocket] Pocket008
  Direction = (0,1,-2e-16)
  Length = 5
  Length2 = 5
  Profile = -> Sketch049
  ReferenceAxis = -> Sketch049 [N_Axis]
  Type = 0
FEATURE [Sketcher::SketchObject] Sketch050
  FullyConstrained = false
  MapMode = 5
  Placement = pos=(0,0,0) rot=(0.57735,-0.57735,-0.57735;2.0944rad)
  Support = -> [Pocket008]
  sketch-geometry (4):
    g0: LineSegment StartX=14.4002 StartY=0 StartZ=0 EndX=109.3 EndY=0 EndZ=0
    g1: LineSegment StartX=109.3 StartY=0 StartZ=0 EndX=109.3 EndY=4 EndZ=0
    g2: LineSegment StartX=109.3 StartY=4 StartZ=0 EndX=14.4002 EndY=4 EndZ=0
    g3: LineSegment StartX=14.4002 StartY=4 StartZ=0 EndX=14.4002 EndY=0 EndZ=0
  constraints (11):
    c: Coincident(g0,g1)
    c: Coincident(g1,g2)
    c: Coincident(g2,g3)
    c: Coincident(g3,g0)
    c: Horizontal(g0)
    c: Horizontal(g2)
    c: Vertical(g1)
    c: Vertical(g3)
    c: PointOnObject(g0,g-1)
    c: DistanceX(g2,g2) = 94.8998
    c: DistanceY(g1,g1) = 4
FEATURE [Part::Extrusion] Extrude027
  Base = -> Sketch050
  Dir = (-1,0,0)
  DirMode = 2
  FaceMakerClass = Part::FaceMakerBullseye
  LengthFwd = 3
  LengthRev = 0
  Solid = true
  Symmetric = false
FEATURE [Sketcher::SketchObject] Sketch051
  FullyConstrained = false
  MapMode = 5
  Placement = pos=(84.2,0,0) rot=(0.57735,0.57735,0.57735;2.0944rad)
  Support = -> [Pocket008]
  sketch-geometry (4):
    g0: LineSegment StartX=-109.302 StartY=0 StartZ=0 EndX=-14.4 EndY=0 EndZ=0
    g1: LineSegment StartX=-14.4 StartY=0 StartZ=0 EndX=-14.4 EndY=4 EndZ=0
    g2: LineSegment StartX=-14.4 StartY=4 StartZ=0 EndX=-109.302 EndY=4 EndZ=0
    g3: LineSegment StartX=-109.302 StartY=4 StartZ=0 EndX=-109.302 EndY=0 EndZ=0
  constraints (11):
    c: Coincident(g0,g1)
    c: Coincident(g1,g2)
    c: Coincident(g2,g3)
    c: Coincident(g3,g0)
    c: Horizontal(g0)
    c: Horizontal(g2)
    c: Vertical(g1)
    c: Vertical(g3)
    c: PointOnObject(g0,g-1)
    c: DistanceX(g2,g2) = 94.9019
    c: DistanceY(g1,g1) = 4
FEATURE [Part::Extrusion] Extrude028
  Base = -> Sketch051
  Dir = (1,0,0)
  DirMode = 2
  FaceMakerClass = Part::FaceMakerBullseye
  LengthFwd = 3
  LengthRev = 0
  Solid = true
  Symmetric = false
FEATURE [App::Part] Part  label="main enclosure"
  Group = -> [Body,Extrude004,Extrude005,Sketch007,Sketch006,Body005,BaseFeature,Sketch009,Sketch027,Extrude017,Sketch028,Sketch029,Hole004,Extrude018,Extrude015,BaseFeature005,Hole002,Sketch024,Sketch023,Sketch025,Sketch026,Sketch034,Extrude016,Hole003,Extrude021,Sketch036,Hole007,Extrude013,Sketch021,Sketch022,Pocket006,Sketch042,BaseFeature007,Extrude014,Pocket,Sketch030,Hole005,Body001,Extrude003,+17 more]
  Origin = -> Origin
FEATURE [App::MeasureDistance] Distance009  label="Distance: 3.00017 mm"
  Distance = 3.00017
  P1 = (0,-109.3,3.96765)
  P2 = (-3,-109.3,3.93616)
FEATURE [App::MeasureDistance] Distance010  label="Distance: 90.20000 mm"
  Distance = 90.2
  P1 = (-3,-109.3,0)
  P2 = (87.2,-109.302,0)
FEATURE [Sketcher::SketchObject] Sketch052
  FullyConstrained = false
  MapMode = 5
  Placement = pos=(0,0,0) rot=(1,0,0;1.5708rad)
  Support = -> [XZ_Plane016]
  sketch-geometry (15):
    g0: LineSegment StartX=-3.3 StartY=-0.3 StartZ=0 EndX=-3.3 EndY=4.3 EndZ=0
    g1: LineSegment StartX=-3.3 StartY=4.3 StartZ=0 EndX=-0.300001 EndY=4.3 EndZ=0
    g2: LineSegment StartX=-0.300001 StartY=4.3 StartZ=0 EndX=-0.300001 EndY=23.08 EndZ=0
    g3: LineSegment StartX=-0.300001 StartY=23.08 StartZ=0 EndX=36.86 EndY=23.08 EndZ=0
    g4: LineSegment StartX=47.46 StartY=23.08 StartZ=0 EndX=84.5 EndY=23.08 EndZ=0
    g5: LineSegment StartX=84.5 StartY=23.08 StartZ=0 EndX=84.5 EndY=4.3 EndZ=0
    g6: LineSegment StartX=84.5 StartY=4.3 StartZ=0 EndX=87.5 EndY=4.3 EndZ=0
    g7: LineSegment StartX=87.5 StartY=4.3 StartZ=0 EndX=87.5 EndY=-0.3 EndZ=0
    g8: LineSegment StartX=87.5 StartY=-0.3 StartZ=0 EndX=-3.3 EndY=-0.3 EndZ=0
    g9: LineSegment StartX=-5.3 StartY=-2.3 StartZ=0 EndX=89.5 EndY=-2.3 EndZ=0
    g10: LineSegment StartX=89.5 StartY=-2.3 StartZ=0 EndX=89.5 EndY=26.19 EndZ=0
    g11: LineSegment StartX=89.5 StartY=26.19 StartZ=0 EndX=47.46 EndY=26.19 EndZ=0
    g12: LineSegment StartX=36.86 StartY=23.08 StartZ=0 EndX=47.46 EndY=23.08 EndZ=0
    g13: LineSegment StartX=-5.3 StartY=-2.3 StartZ=0 EndX=-5.3 EndY=26.19 EndZ=0
    g14: LineSegment StartX=-5.3 StartY=26.19 StartZ=0 EndX=47.46 EndY=26.19 EndZ=0
  constraints (41):
    c: Vertical(g0)
    c: Coincident(g0,g1)
    c: Horizontal(g1)
    c: Coincident(g1,g2)
    c: Vertical(g2)
    c: Coincident(g2,g3)
    c: Horizontal(g3)
    c: Horizontal(g4)
    c: Coincident(g4,g5)
    c: Vertical(g5)
    c: Coincident(g5,g6)
    c: Horizontal(g6)
    c: Coincident(g6,g7)
    c: Vertical(g7)
    c: Coincident(g7,g8)
    c: Coincident(g8,g0)
    c: Horizontal(g8)
    c: DistanceX(g8,g8) = 90.8
    c: DistanceX(g1,g1) = 3
    c: DistanceX(g3,g3) = 37.16
    c: DistanceX(g4,g4) = 37.04
    c: DistanceY(g5,g5) = 18.78
    c: DistanceY(g7,g7) = 4.6
    c: DistanceY(g2,g2) = 18.78
    c: DistanceY(g0,g0) = 4.6
    c: Horizontal(g9)
    c: Coincident(g10,g9)
    c: Vertical(g10)
    c: Coincident(g11,g10)
    c: Horizontal(g11)
    c: Coincident(g3,g12)
    c: Coincident(g12,g4)
    c: DistanceX(g12,g12) = 10.6
    c: DistanceY(g10,g10) = 28.49
    c: Coincident(g9,g13)
    c: Vertical(g13)
    c: Coincident(g13,g14)
    c: Coincident(g14,g11)
    c: Horizontal(g14)
    c: DistanceX(g14,g14) = 52.76
    c: DistanceX(g11,g11) = 42.04
FEATURE [App::MeasureDistance] Distance011  label="Distance: 94.80000 mm"
  Distance = 94.8
  P1 = (89.5,2.74181e-07,-2.3)
  P2 = (-5.3,2.74181e-07,-2.3)
FEATURE [App::MeasureDistance] Distance012  label="Distance: 94.92901 mm"
  Distance = 94.929
  P1 = (0,-109.3,22.6426)
  P2 = (0,-14.3705,22.6545)
FEATURE [App::Part] Part006  label="Batt Measurements"
  Group = -> [Distance,Distance001,Distance002,Distance003,Distance004,Distance005,Distance007,Distance008,Distance009,Distance010,Distance011,Distance012]
  Origin = -> Origin013
FEATURE [Part::Extrusion] Extrude029
  Base = -> Sketch052
  Dir = (0,-1,-2e-16)
  DirMode = 2
  FaceMakerClass = Part::FaceMakerBullseye
  LengthFwd = 127
  LengthRev = 0
  Solid = true
  Symmetric = false
FEATURE [App::Part] Part009  label="Battery"
  Group = -> [Part,Part005,Part007,Part001,Part006]
  Origin = -> Origin017
  Placement = pos=(-143,119.3,2) rot=(0,0,1;0rad)
FEATURE [Sketcher::SketchObject] Sketch053
  FullyConstrained = false
  MapMode = 5
  Placement = pos=(0,-5.8e-15,26.19) rot=(0,0,1;0rad)
  Support = -> [Extrude029]
  sketch-geometry (4):
    g0: LineSegment StartX=36.86 StartY=-118.41 StartZ=0 EndX=47.46 EndY=-118.41 EndZ=0
    g1: LineSegment StartX=47.46 StartY=-118.41 StartZ=0 EndX=47.46 EndY=-124.01 EndZ=0
    g2: LineSegment StartX=47.46 StartY=-124.01 StartZ=0 EndX=36.86 EndY=-124.01 EndZ=0
    g3: LineSegment StartX=36.86 StartY=-124.01 StartZ=0 EndX=36.86 EndY=-118.41 EndZ=0
  constraints (10):
    c: Coincident(g0,g1)
    c: Coincident(g1,g2)
    c: Coincident(g2,g3)
    c: Coincident(g3,g0)
    c: Horizontal(g0)
    c: Horizontal(g2)
    c: Vertical(g1)
    c: Vertical(g3)
    c: DistanceX(g2,g2) = 10.6
    c: DistanceY(g1,g1) = 5.6
FEATURE [PartDesign::FeatureBase] BaseFeature010
  BaseFeature = -> Extrude029
FEATURE [PartDesign::Pocket] Pocket009
  Direction = (0,2e-16,-1)
  Length = 5
  Length2 = 5
  Profile = -> Sketch053
  ReferenceAxis = -> Sketch053 [N_Axis]
  Type = 0
FEATURE [Sketcher::SketchObject] Sketch054
  FullyConstrained = false
  MapMode = 5
  Placement = pos=(0,1e-16,-0.3) rot=(0,0,1;0rad)
  Support = -> [Pocket009]
  sketch-geometry (5):
    g0: LineSegment StartX=0 StartY=-32.0705 StartZ=0 EndX=0 EndY=-26.9205 EndZ=0
    g1: LineSegment StartX=0 StartY=-26.9205 StartZ=0 EndX=84.2 EndY=-26.9205 EndZ=0
    g2: LineSegment StartX=84.2 StartY=-26.9205 StartZ=0 EndX=84.2 EndY=-24.9008 EndZ=0
    g3: LineSegment StartX=84.2 StartY=-24.9008 StartZ=0 EndX=0 EndY=-24.9008 EndZ=0
    g4: LineSegment StartX=0 StartY=-24.9008 StartZ=0 EndX=0 EndY=-26.9205 EndZ=0
  constraints (14):
    c: PointOnObject(g0,g-2)
    c: PointOnObject(g0,g-2)
    c: Coincident(g1,g2)
    c: Coincident(g2,g3)
    c: Coincident(g3,g4)
    c: Coincident(g4,g1)
    c: Horizontal(g1)
    c: Horizontal(g3)
    c: Vertical(g2)
    c: Vertical(g4)
    c: Coincident(g1,g0)
    c: DistanceX(g3,g3) = 84.2
    c: DistanceY(g2,g2) = 2.01974
    c: DistanceY(g0,g0) = 5.15
FEATURE [Part::Extrusion] Extrude030
  Base = -> Sketch054
  Dir = (0,-2e-16,1)
  DirMode = 2
  FaceMakerClass = Part::FaceMakerBullseye
  LengthFwd = 23.38
  LengthRev = 0
  Solid = true
  Symmetric = false
FEATURE [Sketcher::SketchObject] Sketch055
  FullyConstrained = false
  MapMode = 5
  Placement = pos=(0,-24.9008,-5.5e-15) rot=(0,0.707107,0.707107;3.14159rad)
  Support = -> [Extrude030]
  sketch-geometry (4):
    g0: LineSegment StartX=-24.64 StartY=14 StartZ=0 EndX=-7 EndY=14 EndZ=0
    g1: LineSegment StartX=-7 StartY=14 StartZ=0 EndX=-7 EndY=10 EndZ=0
    g2: LineSegment StartX=-7 StartY=10 StartZ=0 EndX=-24.64 EndY=10 EndZ=0
    g3: LineSegment StartX=-24.64 StartY=10 StartZ=0 EndX=-24.64 EndY=14 EndZ=0
  constraints (10):
    c: Coincident(g0,g1)
    c: Coincident(g1,g2)
    c: Coincident(g2,g3)
    c: Coincident(g3,g0)
    c: Horizontal(g0)
    c: Horizontal(g2)
    c: Vertical(g1)
    c: Vertical(g3)
    c: DistanceX(g0,g0) = 17.64
    c: DistanceY(g3,g3) = 4
FEATURE [PartDesign::FeatureBase] BaseFeature011
  BaseFeature = -> Extrude030
FEATURE [PartDesign::Pocket] Pocket010
  Direction = (0,-1,-2e-16)
  Length = 5
  Length2 = 5
  Profile = -> Sketch055
  ReferenceAxis = -> Sketch055 [N_Axis]
  Type = 0
FEATURE [App::MeasureDistance] Distance013  label="Distance: 28.49007 mm"
  Distance = 28.4901
  P1 = (-5.3,-5e-16,-2.3)
  P2 = (-5.3,-0.0648938,26.19)
FEATURE [App::MeasureDistance] Distance014  label="Distance: 126.98823 mm"
  Distance = 126.988
  P1 = (-5.3,-126.988,26.19)
  P2 = (-5.3,5.8e-15,26.19)
FEATURE [TechDraw::DrawSVGTemplate] Template
  EditableTexts = Designed_by_Name=Designed by Name; Drawing_number=Drawing number; FC-Date=Date; FC-SC=Scale; FC-SH=Sheet; FC-Title=Title; Subtitle=Subtitle; Weight=Weight
  Height = 210
  Orientation = 1
  Template = C:/Program Files/FreeCAD 0.21/data/Mod/TechDraw/Templates/A4_LandscapeTD.svg
  Width = 297
FEATURE [Sketcher::SketchObject] Sketch056
  FullyConstrained = false
  MapMode = 5
  Placement = pos=(0,-24.9008,-5.5e-15) rot=(0,0.707107,0.707107;3.14159rad)
  Support = -> [Pocket010]
  sketch-geometry (12):
    g0: LineSegment StartX=-84.2 StartY=-0.3 StartZ=0 EndX=-87.5 EndY=-0.3 EndZ=0
    g1: LineSegment StartX=-87.5 StartY=-0.3 StartZ=0 EndX=-87.5 EndY=4.3 EndZ=0
    g2: LineSegment StartX=-87.5 StartY=4.3 StartZ=0 EndX=-84.5 EndY=4.3 EndZ=0
    g3: LineSegment StartX=-84.5 StartY=4.3 StartZ=0 EndX=-84.5 EndY=23.08 EndZ=0
    g4: LineSegment StartX=-84.5 StartY=23.08 StartZ=0 EndX=-84.2 EndY=23.08 EndZ=0
    g5: LineSegment StartX=-84.2 StartY=23.08 StartZ=0 EndX=-84.2 EndY=-0.3 EndZ=0
    g6: LineSegment StartX=0 StartY=-0.3004 StartZ=0 EndX=3.3 EndY=-0.3004 EndZ=0
    g7: LineSegment StartX=3.3 StartY=-0.3004 StartZ=0 EndX=3.3 EndY=4.3 EndZ=0
    g8: LineSegment StartX=3.3 StartY=4.3 StartZ=0 EndX=0.3 EndY=4.3 EndZ=0
    g9: LineSegment StartX=0.3 StartY=4.3 StartZ=0 EndX=0.3 EndY=23.0798 EndZ=0
    g10: LineSegment StartX=0.3 StartY=23.0798 StartZ=0 EndX=0 EndY=23.0798 EndZ=0
    g11: LineSegment StartX=0 StartY=23.0798 StartZ=0 EndX=0 EndY=-0.3004 EndZ=0
  constraints (33):
    c: Horizontal(g0)
    c: Coincident(g0,g1)
    c: Vertical(g1)
    c: Coincident(g1,g2)
    c: Horizontal(g2)
    c: Coincident(g2,g3)
    c: Vertical(g3)
    c: Coincident(g3,g4)
    c: Horizontal(g4)
    c: Coincident(g4,g5)
    c: Coincident(g5,g0)
    c: Vertical(g5)
    c: DistanceX(g0,g0) = 3.3
    c: DistanceY(g5,g5) = 23.38
    c: DistanceY(g1,g1) = 4.6
    c: DistanceX(g2,g2) = 3
    c: PointOnObject(g6,g-2)
    c: Horizontal(g6)
    c: Coincident(g6,g7)
    c: Vertical(g7)
    c: Coincident(g7,g8)
    c: Horizontal(g8)
    c: Coincident(g8,g9)
    c: Vertical(g9)
    c: Coincident(g9,g10)
    c: PointOnObject(g10,g-2)
    c: Horizontal(g10)
    c: Coincident(g10,g11)
    c: Coincident(g11,g6)
    c: DistanceY(g11,g11) = 23.3802
    c: DistanceX(g6,g6) = 3.3
    c: DistanceX(g8,g8) = 3
    c: DistanceY(g7,g7) = 4.6004
FEATURE [Part::Extrusion] Extrude031
  Base = -> Sketch056
  Dir = (0,1,2e-16)
  DirMode = 2
  FaceMakerClass = Part::FaceMakerBullseye
  LengthFwd = 2
  LengthRev = 0
  Solid = true
  Symmetric = false
FEATURE [App::MeasureDistance] Distance015  label="Distance: 5.00009 mm"
  Distance = 5.00009
  P1 = (84.5,1e-15,4.3)
  P2 = (89.5,1e-15,4.33063)
FEATURE [App::MeasureDistance] Distance016  label="Distance: 22.77007 mm"
  Distance = 22.7701
  P1 = (-3.21781,-22.77,-0.3)
  P2 = (-3.27073,-1e-16,-0.3)
FEATURE [App::MeasureDistance] Distance017  label="Distance: 2.00024 mm"
  Distance = 2.00024
  P1 = (0,-22.9008,-0.289555)
  P2 = (0.0308171,-24.9008,-0.293916)
FEATURE [App::MeasureDistance] Distance018  label="Distance: 3.11947 mm"
  Distance = 3.11947
  P1 = (84.5029,5.2e-15,23.0706)
  P2 = (84.5234,5.8e-15,26.19)
FEATURE [App::MeasureDistance] Distance019  label="Distance: 4.60003 mm"
  Distance = 4.60003
  P1 = (-3.3,-1e-16,-0.3)
  P2 = (-3.28346,1e-15,4.3)
FEATURE [App::MeasureDistance] Distance020  label="Distance: 18.78000 mm"
  Distance = 18.78
  P1 = (-0.300001,1e-15,4.3)
  P2 = (-0.300001,5.1e-15,23.08)
FEATURE [App::Part] Part010  label="internal sleeve measurements"
  Group = -> [Distance014,Distance013,Distance015,Distance016,Distance017,Distance018,Distance019,Distance020]
  Origin = -> Origin018
FEATURE [Sketcher::SketchObject] Sketch057  label="right side screw holes"
  FullyConstrained = false
  MapMode = 5
  Placement = pos=(84.5,0,0) rot=(0.57735,-0.57735,-0.57735;2.0944rad)
  Support = -> [Pocket009]
  sketch-geometry (21):
    g0: LineSegment StartX=127 StartY=4.27233 StartZ=0 EndX=127 EndY=22.9667 EndZ=0
    g1: LineSegment StartX=127 StartY=4.29202 StartZ=0 EndX=127 EndY=13.292 EndZ=0
    g2: LineSegment StartX=127 StartY=13.292 StartZ=0 EndX=26.92 EndY=13.292 EndZ=0
    g3: LineSegment StartX=127.04 StartY=4.3 StartZ=0 EndX=127.04 EndY=8.79999 EndZ=0
    g4: LineSegment StartX=127.04 StartY=8.79999 StartZ=0 EndX=127 EndY=8.79999 EndZ=0
    g5: LineSegment StartX=127 StartY=8.79999 StartZ=0 EndX=122.5 EndY=8.79999 EndZ=0
    g6: LineSegment StartX=127 StartY=22.9667 StartZ=0 EndX=127 EndY=18.3926 EndZ=0
    g7: LineSegment StartX=127 StartY=18.3926 StartZ=0 EndX=122.5 EndY=18.3926 EndZ=0
    g8: LineSegment StartX=122.5 StartY=8.79999 StartZ=0 EndX=122.5 EndY=13.292 EndZ=0
    g9: LineSegment StartX=122.5 StartY=13.292 StartZ=0 EndX=104.494 EndY=13.292 EndZ=0
    g10: LineSegment StartX=104.494 StartY=13.292 StartZ=0 EndX=86.49 EndY=13.292 EndZ=0
    g11: LineSegment StartX=86.49 StartY=13.292 StartZ=0 EndX=68.4897 EndY=13.292 EndZ=0
    g12: LineSegment StartX=68.4897 StartY=13.292 StartZ=0 EndX=50.4896 EndY=13.292 EndZ=0
    g13: LineSegment StartX=50.4896 StartY=13.292 StartZ=0 EndX=32.4898 EndY=13.292 EndZ=0
    g14: Circle CenterX=122.5 CenterY=18.3926 CenterZ=0 NormalX=0 NormalY=0 NormalZ=1 AngleXU=0 Radius=2.55
    g15: Circle CenterX=122.5 CenterY=8.79999 CenterZ=0 NormalX=0 NormalY=0 NormalZ=1 AngleXU=0 Radius=2.55
    g16: Circle CenterX=104.494 CenterY=13.292 CenterZ=0 NormalX=0 NormalY=0 NormalZ=1 AngleXU=0 Radius=2.55
    g17: Circle CenterX=86.49 CenterY=13.292 CenterZ=0 NormalX=0 NormalY=0 NormalZ=1 AngleXU=0 Radius=2.55
    g18: Circle CenterX=68.4897 CenterY=13.292 CenterZ=0 NormalX=0 NormalY=0 NormalZ=1 AngleXU=0 Radius=2.55
    g19: Circle CenterX=32.4898 CenterY=13.292 CenterZ=0 NormalX=0 NormalY=0 NormalZ=1 AngleXU=0 Radius=2.55
    g20: Circle CenterX=50.4896 CenterY=13.292 CenterZ=0 NormalX=0 NormalY=0 NormalZ=1 AngleXU=0 Radius=2.55
  constraints (44):
    c: Vertical(g0)
    c: DistanceY(g0,g0) = 18.6944
    c: Vertical(g1)
    c: DistanceY(g1,g1) = 9
    c: Coincident(g2,g1)
    c: Horizontal(g2)
    c: DistanceX(g2,g2) = 100.08
    c: Vertical(g3)
    c: Coincident(g4,g3)
    c: PointOnObject(g4,g0)
    c: Horizontal(g4)
    c: Coincident(g5,g4)
    c: Horizontal(g5)
    c: PointOnObject(g6,g0)
    c: Vertical(g6)
    c: Coincident(g7,g6)
    c: Horizontal(g7)
    c: Coincident(g5,g8)
    c: PointOnObject(g8,g2)
    c: Vertical(g8)
    c: Coincident(g8,g9)
    c: PointOnObject(g9,g2)
    c: Coincident(g9,g10)
    c: PointOnObject(g10,g2)
    c: Coincident(g10,g11)
    c: PointOnObject(g11,g2)
    c: Coincident(g11,g12)
    c: PointOnObject(g12,g2)
    c: Coincident(g12,g13)
    c: PointOnObject(g13,g2)
    c: Coincident(g14,g7)
    c: Coincident(g15,g5)
    c: Coincident(g16,g9)
    c: Coincident(g17,g10)
    c: Coincident(g18,g11)
    c: Coincident(g19,g13)
    c: Diameter(g19) = 5.1
    c: Diameter(g18) = 5.1
    c: Diameter(g17) = 5.1
    c: Diameter(g16) = 5.1
    c: Diameter(g14) = 5.1
    c: Diameter(g15) = 5.1
    c: Coincident(g20,g12)
    c: Diameter(g20) = 5.1
FEATURE [PartDesign::Hole] Hole010
  CustomThreadClearance = 0
  Depth = 25
  DepthType = 0
  Diameter = 3.1
  DrillForDepth = false
  DrillPoint = 0
  DrillPointAngle = 118
  HoleCutCountersinkAngle = 90
  HoleCutCustomValues = false
  HoleCutDepth = 2.3
  HoleCutDiameter = 5.1
  HoleCutType = 2
  ModelThread = false
  Profile = -> Sketch057
  Tapered = false
  TaperedAngle = 90
  ThreadClass = 0
  ThreadDepth = 25
  ThreadDepthType = 0
  ThreadDirection = 0
  ThreadFit = 0
  ThreadSize = 0
  ThreadType = 0
  Threaded = false
  UseCustomThreadClearance = false
FEATURE [Sketcher::SketchObject] MirroredSketch  label="left side screw holes"
  FullyConstrained = false
  Placement = pos=(-0.300001,0,0) rot=(0.57735,0.57735,0.57735;2.0944rad)
  sketch-geometry (21):
    g0: LineSegment StartX=-127 StartY=4.27233 StartZ=0 EndX=-127 EndY=22.9667 EndZ=0
    g1: LineSegment StartX=-127 StartY=4.29202 StartZ=0 EndX=-127 EndY=13.292 EndZ=0
    g2: LineSegment StartX=-127 StartY=13.292 StartZ=0 EndX=-26.92 EndY=13.292 EndZ=0
    g3: LineSegment StartX=-127.04 StartY=4.3 StartZ=0 EndX=-127.04 EndY=8.79999 EndZ=0
    g4: LineSegment StartX=-127.04 StartY=8.79999 StartZ=0 EndX=-127 EndY=8.79999 EndZ=0
    g5: LineSegment StartX=-127 StartY=8.79999 StartZ=0 EndX=-122.5 EndY=8.79999 EndZ=0
    g6: LineSegment StartX=-127 StartY=22.9667 StartZ=0 EndX=-127 EndY=18.3926 EndZ=0
    g7: LineSegment StartX=-127 StartY=18.3926 StartZ=0 EndX=-122.5 EndY=18.3926 EndZ=0
    g8: LineSegment StartX=-122.5 StartY=8.79999 StartZ=0 EndX=-122.5 EndY=13.292 EndZ=0
    g9: LineSegment StartX=-122.5 StartY=13.292 StartZ=0 EndX=-104.494 EndY=13.292 EndZ=0
    g10: LineSegment StartX=-104.494 StartY=13.292 StartZ=0 EndX=-86.49 EndY=13.292 EndZ=0
    g11: LineSegment StartX=-86.49 StartY=13.292 StartZ=0 EndX=-68.4897 EndY=13.292 EndZ=0
    g12: LineSegment StartX=-68.4897 StartY=13.292 StartZ=0 EndX=-50.4896 EndY=13.292 EndZ=0
    g13: LineSegment StartX=-50.4896 StartY=13.292 StartZ=0 EndX=-32.4898 EndY=13.292 EndZ=0
    g14: Circle CenterX=-122.5 CenterY=18.3926 CenterZ=0 NormalX=0 NormalY=0 NormalZ=1 AngleXU=0 Radius=2.55
    g15: Circle CenterX=-122.5 CenterY=8.79999 CenterZ=0 NormalX=0 NormalY=0 NormalZ=1 AngleXU=0 Radius=2.55
    g16: Circle CenterX=-104.494 CenterY=13.292 CenterZ=0 NormalX=0 NormalY=0 NormalZ=1 AngleXU=0 Radius=2.55
    g17: Circle CenterX=-86.49 CenterY=13.292 CenterZ=0 NormalX=0 NormalY=0 NormalZ=1 AngleXU=0 Radius=2.55
    g18: Circle CenterX=-68.4897 CenterY=13.292 CenterZ=0 NormalX=0 NormalY=0 NormalZ=1 AngleXU=0 Radius=2.55
    g19: Circle CenterX=-32.4898 CenterY=13.292 CenterZ=0 NormalX=0 NormalY=0 NormalZ=1 AngleXU=0 Radius=2.55
    g20: Circle CenterX=-50.4896 CenterY=13.292 CenterZ=0 NormalX=0 NormalY=0 NormalZ=1 AngleXU=0 Radius=2.55
  constraints (41):
    c: Vertical(g0)
    c: Vertical(g1)
    c: Coincident(g2,g1)
    c: Horizontal(g2)
    c: Vertical(g3)
    c: Coincident(g4,g3)
    c: PointOnObject(g4,g0)
    c: Horizontal(g4)
    c: Coincident(g5,g4)
    c: Horizontal(g5)
    c: PointOnObject(g6,g0)
    c: Vertical(g6)
    c: Coincident(g7,g6)
    c: Horizontal(g7)
    c: Coincident(g5,g8)
    c: PointOnObject(g8,g2)
    c: Vertical(g8)
    c: Coincident(g8,g9)
    c: PointOnObject(g9,g2)
    c: Coincident(g9,g10)
    c: PointOnObject(g10,g2)
    c: Coincident(g10,g11)
    c: PointOnObject(g11,g2)
    c: Coincident(g11,g12)
    c: PointOnObject(g12,g2)
    c: Coincident(g12,g13)
    c: PointOnObject(g13,g2)
    c: Coincident(g14,g7)
    c: Coincident(g15,g5)
    c: Coincident(g16,g9)
    c: Coincident(g17,g10)
    c: Coincident(g18,g11)
    c: Coincident(g19,g13)
    c: Diameter(g19) = 5.1
    c: Diameter(g18) = 5.1
    c: Diameter(g17) = 5.1
    c: Diameter(g16) = 5.1
    c: Diameter(g14) = 5.1
    c: Diameter(g15) = 5.1
    c: Coincident(g20,g12)
    c: Diameter(g20) = 5.1
FEATURE [PartDesign::Hole] Hole011
  BaseFeature = -> Hole010
  CustomThreadClearance = 0
  Depth = 25
  DepthType = 0
  Diameter = 3.1
  DrillForDepth = false
  DrillPoint = 0
  DrillPointAngle = 118
  HoleCutCountersinkAngle = 90
  HoleCutCustomValues = false
  HoleCutDepth = 2.3
  HoleCutDiameter = 5.1
  HoleCutType = 2
  ModelThread = false
  Profile = -> MirroredSketch
  Tapered = false
  TaperedAngle = 90
  ThreadClass = 0
  ThreadDepth = 25
  ThreadDepthType = 0
  ThreadDirection = 0
  ThreadFit = 0
  ThreadSize = 0
  ThreadType = 0
  Threaded = false
  UseCustomThreadClearance = false
FEATURE [Sketcher::SketchObject] Sketch058  label="base mounting holes"
  FullyConstrained = false
  MapMode = 5
  Placement = pos=(0,1e-16,-0.3) rot=(0,0,1;0rad)
  Support = -> [Hole011]
  sketch-geometry (21):
    g0: LineSegment StartX=-3.39232 StartY=-126.994 StartZ=0 EndX=-0.3 EndY=-126.994 EndZ=0
    g1: LineSegment StartX=-0.3 StartY=-126.994 StartZ=0 EndX=87.4321 EndY=-126.994 EndZ=0
    g2: LineSegment StartX=84.4483 StartY=-126.994 StartZ=0 EndX=87.4321 EndY=-126.994 EndZ=0
    g3: LineSegment StartX=-0.3 StartY=-126.994 StartZ=0 EndX=-0.3 EndY=-26.8938 EndZ=0
    g4: LineSegment StartX=-0.3 StartY=-126.994 StartZ=0 EndX=-0.3 EndY=-122.493 EndZ=0
    g5: LineSegment StartX=-0.3 StartY=-122.493 StartZ=0 EndX=4.20453 EndY=-122.493 EndZ=0
    g6: LineSegment StartX=4.20453 StartY=-122.493 StartZ=0 EndX=23.1295 EndY=-122.493 EndZ=0
    g7: LineSegment StartX=23.1299 StartY=-122.493 StartZ=0 EndX=42.0549 EndY=-122.493 EndZ=0
    g8: LineSegment StartX=42.0549 StartY=-122.493 StartZ=0 EndX=60.9799 EndY=-122.493 EndZ=0
    g9: LineSegment StartX=60.98 StartY=-122.493 StartZ=0 EndX=79.905 EndY=-122.493 EndZ=0
    g10: LineSegment StartX=84.4483 StartY=-126.994 StartZ=0 EndX=84.4483 EndY=-122.493 EndZ=0
    g11: LineSegment StartX=79.905 StartY=-122.493 StartZ=0 EndX=84.4483 EndY=-122.493 EndZ=0
    g12: LineSegment StartX=23.1295 StartY=-122.493 StartZ=0 EndX=23.1295 EndY=-92.4 EndZ=0
    g13: LineSegment StartX=60.9799 StartY=-122.493 StartZ=0 EndX=60.9799 EndY=-92.4 EndZ=0
    g14: Circle CenterX=4.20453 CenterY=-122.493 CenterZ=0 NormalX=0 NormalY=0 NormalZ=1 AngleXU=0 Radius=2.55
    g15: Circle CenterX=23.1299 CenterY=-122.493 CenterZ=0 NormalX=0 NormalY=0 NormalZ=1 AngleXU=0 Radius=2.55
    g16: Circle CenterX=42.0549 CenterY=-122.493 CenterZ=0 NormalX=0 NormalY=0 NormalZ=1 AngleXU=0 Radius=2.55
    g17: Circle CenterX=60.9799 CenterY=-122.493 CenterZ=0 NormalX=0 NormalY=0 NormalZ=1 AngleXU=0 Radius=2.55
    g18: Circle CenterX=79.905 CenterY=-122.493 CenterZ=0 NormalX=0 NormalY=0 NormalZ=1 AngleXU=0 Radius=2.55
    g19: Circle CenterX=60.9799 CenterY=-92.4 CenterZ=0 NormalX=0 NormalY=0 NormalZ=1 AngleXU=0 Radius=2.55
    g20: Circle CenterX=23.1295 CenterY=-92.4 CenterZ=0 NormalX=0 NormalY=0 NormalZ=1 AngleXU=0 Radius=2.55
  constraints (52):
    c: Horizontal(g0)
    c: Coincident(g0,g1)
    c: Horizontal(g1)
    c: PointOnObject(g2,g1)
    c: Coincident(g2,g1)
    c: DistanceX(g1,g1) = 87.7321
    c: DistanceX(g0,g0) = 3.09232
    c: Coincident(g0,g3)
    c: Vertical(g3)
    c: DistanceY(g3,g3) = 100.1
    c: Coincident(g4,g0)
    c: PointOnObject(g4,g3)
    c: DistanceY(g4,g4) = 4.50086
    c: Coincident(g4,g5)
    c: Horizontal(g5)
    c: DistanceX(g5,g5) = 4.50453
    c: Coincident(g5,g6)
    c: Horizontal(g6)
    c: DistanceX(g6,g6) = 18.925
    c: Horizontal(g7)
    c: DistanceX(g7,g7) = 18.925
    c: Horizontal(g8)
    c: DistanceX(g8,g8) = 18.925
    c: Horizontal(g9)
    c: DistanceX(g9,g9) = 18.925
    c: DistanceX(g2,g2) = 2.98381
    c: Coincident(g10,g2)
    c: Vertical(g10)
    c: Coincident(g11,g9)
    c: Coincident(g11,g10)
    c: Horizontal(g11)
    c: DistanceX(g11,g11) = 4.54329
    c: Coincident(g12,g6)
    c: Vertical(g12)
    c: Coincident(g13,g8)
    c: Vertical(g13)
    c: DistanceY(g12,g12) = 30.0929
    c: DistanceY(g13,g13) = 30.093
    c: Coincident(g14,g5)
    c: Coincident(g15,g7)
    c: Coincident(g16,g7)
    c: Coincident(g17,g8)
    c: Coincident(g18,g9)
    c: Coincident(g19,g13)
    c: Coincident(g20,g12)
    c: Diameter(g20) = 5.1
    c: Diameter(g19) = 5.1
    c: Diameter(g16) = 5.1
    c: Diameter(g15) = 5.1
    c: Diameter(g14) = 5.1
    c: Diameter(g17) = 5.1
    c: Diameter(g18) = 5.1
FEATURE [PartDesign::Hole] Hole012
  BaseFeature = -> Hole011
  CustomThreadClearance = 0
  Depth = 25
  DepthType = 0
  Diameter = 3.1
  DrillForDepth = false
  DrillPoint = 0
  DrillPointAngle = 118
  HoleCutCountersinkAngle = 90
  HoleCutCustomValues = false
  HoleCutDepth = 2.3
  HoleCutDiameter = 5.1
  HoleCutType = 2
  ModelThread = false
  Profile = -> Sketch058
  Tapered = false
  TaperedAngle = 90
  ThreadClass = 0
  ThreadDepth = 25
  ThreadDepthType = 0
  ThreadDirection = 0
  ThreadFit = 0
  ThreadSize = 0
  ThreadType = 0
  Threaded = false
  UseCustomThreadClearance = false
FEATURE [Sketcher::SketchObject] Sketch060
  FullyConstrained = false
  MapMode = 5
  Placement = pos=(0,-5.1e-15,23.08) rot=(1,0,0;3.14159rad)
  Support = -> [Hole012]
  sketch-geometry (7):
    g0: Circle CenterX=4.2 CenterY=122.5 CenterZ=0 NormalX=0 NormalY=0 NormalZ=1 AngleXU=0 Radius=2.55
    g1: Circle CenterX=23.1306 CenterY=122.5 CenterZ=0 NormalX=0 NormalY=0 NormalZ=1 AngleXU=0 Radius=2.55
    g2: Circle CenterX=42.0697 CenterY=110.4 CenterZ=0 NormalX=0 NormalY=0 NormalZ=1 AngleXU=0 Radius=2.55
    g3: Circle CenterX=61 CenterY=122.463 CenterZ=0 NormalX=0 NormalY=0 NormalZ=1 AngleXU=0 Radius=2.55
    g4: Circle CenterX=79.9 CenterY=122.5 CenterZ=0 NormalX=0 NormalY=0 NormalZ=1 AngleXU=0 Radius=2.55
    g5: Circle CenterX=60.9712 CenterY=92.4 CenterZ=0 NormalX=0 NormalY=0 NormalZ=1 AngleXU=0 Radius=2.55
    g6: Circle CenterX=23.1258 CenterY=92.4 CenterZ=0 NormalX=0 NormalY=0 NormalZ=1 AngleXU=0 Radius=2.55
  constraints (7):
    c: Diameter(g0) = 5.1
    c: Diameter(g1) = 5.1
    c: Diameter(g3) = 5.1
    c: Diameter(g4) = 5.1
    c: Diameter(g2) = 5.1
    c: Diameter(g6) = 5.1
    c: Diameter(g5) = 5.1
FEATURE [PartDesign::Hole] Hole013
  BaseFeature = -> Hole012
  CustomThreadClearance = 0
  Depth = 25
  DepthType = 0
  Diameter = 3.1
  DrillForDepth = false
  DrillPoint = 0
  DrillPointAngle = 118
  HoleCutCountersinkAngle = 90
  HoleCutCustomValues = false
  HoleCutDepth = 2.3
  HoleCutDiameter = 5.1
  HoleCutType = 2
  ModelThread = false
  Profile = -> Sketch060
  Tapered = false
  TaperedAngle = 90
  ThreadClass = 0
  ThreadDepth = 25
  ThreadDepthType = 0
  ThreadDirection = 0
  ThreadFit = 0
  ThreadSize = 0
  ThreadType = 0
  Threaded = false
  UseCustomThreadClearance = false
FEATURE [Sketcher::SketchObject] Sketch061
  FullyConstrained = false
  MapMode = 5
  Placement = pos=(0,0,0) rot=(0,0.707107,0.707107;3.14159rad)
  Support = -> [Hole013]
  sketch-geometry (4):
    g0: Circle CenterX=-87 CenterY=8 CenterZ=0 NormalX=0 NormalY=0 NormalZ=1 AngleXU=0 Radius=1.5
    g1: Circle CenterX=-87 CenterY=24 CenterZ=0 NormalX=0 NormalY=0 NormalZ=1 AngleXU=0 Radius=1.5
    g2: Circle CenterX=3 CenterY=24 CenterZ=0 NormalX=0 NormalY=0 NormalZ=1 AngleXU=0 Radius=1.5
    g3: Circle CenterX=3 CenterY=8 CenterZ=0 NormalX=0 NormalY=0 NormalZ=1 AngleXU=0 Radius=1.5
  constraints (4):
    c: Diameter(g0) = 3
    c: Diameter(g1) = 3
    c: Diameter(g2) = 3
    c: Diameter(g3) = 3
FEATURE [PartDesign::Hole] Hole014
  BaseFeature = -> Hole013
  CustomThreadClearance = 0
  Depth = 2.5
  DepthType = 0
  Diameter = 3.2
  DrillForDepth = false
  DrillPoint = 0
  DrillPointAngle = 118
  HoleCutCountersinkAngle = 90
  HoleCutCustomValues = false
  HoleCutDepth = 0
  HoleCutDiameter = 6.1
  HoleCutType = 0
  ModelThread = false
  Profile = -> Sketch061
  Tapered = false
  TaperedAngle = 90
  ThreadClass = 0
  ThreadDepth = 2.5
  ThreadDepthType = 0
  ThreadDirection = 0
  ThreadFit = 0
  ThreadSize = 0
  ThreadType = 0
  Threaded = false
  UseCustomThreadClearance = false
FEATURE [PartDesign::Body] Body007  label="exterior sleeve"
  Group = -> [Sketch057,Hole010,MirroredSketch,Hole011,Sketch058,Hole012,Sketch060,Hole013,Sketch061,Hole014]
  Origin = -> Origin016
  Tip = -> Hole014
FEATURE [App::Part] Part008  label="sleeve enclosure"
  Group = -> [Body007,BaseFeature010,Extrude030,BaseFeature011,Sketch052,Sketch053,Sketch054,Sketch055,Pocket010,Pocket009,Sketch056,Extrude031]
  Origin = -> Origin015
FEATURE [TechDraw::DrawViewPart] View
  CoarseView = false
  Direction = (-0.481376,0.876256,-0.021278)
  Focus = 100
  HardHidden = false
  IsoCount = 0
  IsoHidden = false
  IsoVisible = false
  LockPosition = false
  Perspective = false
  Rotation = 0
  ScaleType = 0
  ScrubCount = 0
  SeamHidden = false
  SeamVisible = false
  SmoothHidden = false
  SmoothVisible = true
  Source = -> [Part008]
  X = 100.661
  XDirection = (-0.875359,-0.481846,-0.0396472)
  Y = 158.972
FEATURE [TechDraw::DrawViewDimension] Dimension001
  AngleOverride = false
  Arbitrary = false
  ArbitraryTolerances = false
  EqualTolerance = true
  ExtensionAngle = 0
  FormatSpec = %.2w
  FormatSpecOverTolerance = %+.2w
  FormatSpecUnderTolerance = %+.2w
  Inverted = false
  LineAngle = 0
  LockPosition = false
  MeasureType = 1
  OverTolerance = 0
  References2D = -> [View]
  Rotation = 0
  ScaleType = 0
  TheoreticalExact = false
  Type = 2
  UnderTolerance = 0
  X = 81.8498
  Y = 4.95765
FEATURE [TechDraw::DrawViewDimension] Dimension
  AngleOverride = false
  Arbitrary = false
  ArbitraryTolerances = false
  EqualTolerance = true
  ExtensionAngle = 0
  FormatSpec = %.2w
  FormatSpecOverTolerance = %+.2w
  FormatSpecUnderTolerance = %+.2w
  Inverted = false
  LineAngle = 0
  LockPosition = false
  MeasureType = 1
  OverTolerance = 0
  References2D = -> [View]
  Rotation = 0
  ScaleType = 0
  TheoreticalExact = false
  Type = 1
  UnderTolerance = 0
  X = 32.2763
  Y = -17.3846
FEATURE [TechDraw::DrawPage] Page
  KeepUpdated = true
  NextBalloonIndex = 1
  ProjectionType = 0
  Template = -> Template
  Views = -> [View,Dimension001,Dimension]
FEATURE [App::Part] Part011  label="Internal Sleeve"
  Group = -> [Part008,Part010]
  Origin = -> Origin019
FEATURE [App::Part] Part012  label="Technical Docs"
  Group = -> [Page,Dimension]
  Origin = -> Origin020
FEATURE [Sketcher::SketchObject] Sketch062
  FullyConstrained = false
  MapMode = 5
  Support = -> [XY_Plane021]
  sketch-geometry (4):
    g0: LineSegment StartX=-5.3 StartY=10 StartZ=0 EndX=89.5 EndY=10 EndZ=0
    g1: LineSegment StartX=89.5 StartY=10 StartZ=0 EndX=89.5 EndY=137 EndZ=0
    g2: LineSegment StartX=89.5 StartY=137 StartZ=0 EndX=-5.3 EndY=137 EndZ=0
    g3: LineSegment StartX=-5.3 StartY=137 StartZ=0 EndX=-5.3 EndY=10 EndZ=0
  constraints (10):
    c: Coincident(g0,g1)
    c: Coincident(g1,g2)
    c: Coincident(g2,g3)
    c: Coincident(g3,g0)
    c: Horizontal(g0)
    c: Horizontal(g2)
    c: Vertical(g1)
    c: Vertical(g3)
    c: DistanceX(g2,g2) = 94.8
    c: DistanceY(g3,g3) = 127
FEATURE [PartDesign::Pad] Pad
  Direction = (0,0,1)
  Length = 28.5
  Length2 = 10
  Profile = -> Sketch062
  ReferenceAxis = -> Sketch062 [N_Axis]
  Type = 0
FEATURE [Sketcher::SketchObject] Sketch063
  FullyConstrained = false
  MapMode = 5
  Placement = pos=(0,10,0) rot=(1,0,0;1.5708rad)
  Support = -> [Pad]
  sketch-geometry (8):
    g0: LineSegment StartX=-3.3 StartY=2.01 StartZ=0 EndX=-3.3 EndY=6.61 EndZ=0
    g1: LineSegment StartX=-3.3 StartY=6.61 StartZ=0 EndX=-0.299998 EndY=6.61 EndZ=0
    g2: LineSegment StartX=-0.299998 StartY=6.61 StartZ=0 EndX=-0.299998 EndY=25.39 EndZ=0
    g3: LineSegment StartX=84.5 StartY=25.39 StartZ=0 EndX=84.5 EndY=6.61 EndZ=0
    g4: LineSegment StartX=84.5 StartY=6.61 StartZ=0 EndX=87.5 EndY=6.61 EndZ=0
    g5: LineSegment StartX=87.5 StartY=6.61 StartZ=0 EndX=87.5 EndY=2.01 EndZ=0
    g6: LineSegment StartX=87.5 StartY=2.01 StartZ=0 EndX=-3.3 EndY=2.01 EndZ=0
    g7: LineSegment StartX=-0.299998 StartY=25.39 StartZ=0 EndX=84.5 EndY=25.39 EndZ=0
  constraints (22):
    c: Vertical(g0)
    c: Coincident(g0,g1)
    c: Horizontal(g1)
    c: Coincident(g1,g2)
    c: Vertical(g2)
    c: Vertical(g3)
    c: Coincident(g3,g4)
    c: Horizontal(g4)
    c: Coincident(g4,g5)
    c: Vertical(g5)
    c: Coincident(g5,g6)
    c: Coincident(g6,g0)
    c: Horizontal(g6)
    c: DistanceX(g6,g6) = 90.8
    c: DistanceX(g1,g1) = 3
    c: DistanceY(g3,g3) = 18.78
    c: DistanceY(g5,g5) = 4.6
    c: DistanceY(g2,g2) = 18.78
    c: DistanceY(g0,g0) = 4.6
    c: Coincident(g7,g2)
    c: Coincident(g7,g3)
    c: DistanceX(g7,g7) = 84.8
FEATURE [PartDesign::Pocket] Pocket011
  BaseFeature = -> Pad
  Direction = (0,1,-2e-16)
  Length = 100
  Length2 = 5
  Profile = -> Sketch063
  ReferenceAxis = -> Sketch063 [N_Axis]
  Type = 0
FEATURE [Sketcher::SketchObject] Sketch064
  FullyConstrained = false
  MapMode = 5
  Placement = pos=(0,137,0) rot=(0,0.707107,0.707107;3.14159rad)
  Support = -> [Pocket011]
  sketch-geometry (4):
    g0: LineSegment StartX=-85.5 StartY=25.38 StartZ=0 EndX=1.3 EndY=25.38 EndZ=0
    g1: LineSegment StartX=1.3 StartY=25.38 StartZ=0 EndX=1.3 EndY=2 EndZ=0
    g2: LineSegment StartX=1.3 StartY=2 StartZ=0 EndX=-85.5 EndY=2 EndZ=0
    g3: LineSegment StartX=-85.5 StartY=2 StartZ=0 EndX=-85.5 EndY=25.38 EndZ=0
  constraints (10):
    c: Coincident(g0,g1)
    c: Coincident(g1,g2)
    c: Coincident(g2,g3)
    c: Coincident(g3,g0)
    c: Horizontal(g0)
    c: Horizontal(g2)
    c: Vertical(g1)
    c: Vertical(g3)
    c: DistanceY(g3,g3) = 23.38
    c: DistanceX(g2,g2) = 86.8
FEATURE [PartDesign::Pocket] Pocket012
  BaseFeature = -> Pocket011
  Direction = (0,-1,2e-16)
  Length = 25
  Length2 = 5
  Profile = -> Sketch064
  ReferenceAxis = -> Sketch064 [N_Axis]
  Type = 0
FEATURE [Sketcher::SketchObject] Sketch065
  FullyConstrained = false
  MapMode = 5
  Placement = pos=(0,0,28.5) rot=(0,0,1;0rad)
  Support = -> [Pocket012]
  sketch-geometry (4):
    g0: LineSegment StartX=-6.21924 StartY=137.919 StartZ=0 EndX=90.5808 EndY=137.919 EndZ=0
    g1: LineSegment StartX=90.5808 StartY=137.919 StartZ=0 EndX=90.5808 EndY=8.91924 EndZ=0
    g2: LineSegment StartX=90.5808 StartY=8.91924 StartZ=0 EndX=-6.21924 EndY=8.91924 EndZ=0
    g3: LineSegment StartX=-6.21924 StartY=8.91924 StartZ=0 EndX=-6.21924 EndY=137.919 EndZ=0
  constraints (10):
    c: Coincident(g0,g1)
    c: Coincident(g1,g2)
    c: Coincident(g2,g3)
    c: Coincident(g3,g0)
    c: Horizontal(g0)
    c: Horizontal(g2)
    c: Vertical(g1)
    c: Vertical(g3)
    c: DistanceX(g0,g0) = 96.8
    c: DistanceY(g3,g3) = 129
FEATURE [PartDesign::Pocket] Pocket013
  BaseFeature = -> Pocket012
  Direction = (0,0,-1)
  Length = 3.2
  Length2 = 5
  Profile = -> Sketch065
  ReferenceAxis = -> Sketch065 [N_Axis]
  Type = 0
FEATURE [Sketcher::SketchObject] Sketch066
  FullyConstrained = false
  MapMode = 5
  Placement = pos=(-5.3,0,0) rot=(0.57735,-0.57735,-0.57735;2.0944rad)
  Support = -> [Pocket013]
  sketch-geometry (4):
    g0: LineSegment StartX=-137 StartY=25.3 StartZ=0 EndX=-10 EndY=25.3 EndZ=0
    g1: LineSegment StartX=-10 StartY=25.3 StartZ=0 EndX=-10 EndY=22.3 EndZ=0
    g2: LineSegment StartX=-10 StartY=22.3 StartZ=0 EndX=-137 EndY=22.3 EndZ=0
    g3: LineSegment StartX=-137 StartY=22.3 StartZ=0 EndX=-137 EndY=25.3 EndZ=0
  constraints (10):
    c: Coincident(g0,g1)
    c: Coincident(g1,g2)
    c: Coincident(g2,g3)
    c: Coincident(g3,g0)
    c: Horizontal(g0)
    c: Horizontal(g2)
    c: Vertical(g1)
    c: Vertical(g3)
    c: DistanceX(g0,g0) = 127
    c: DistanceY(g3,g3) = 3
FEATURE [PartDesign::Pad] Pad001
  BaseFeature = -> Pocket013
  Direction = (-1,0,0)
  Length = 9
  Length2 = 10
  Profile = -> Sketch066
  ReferenceAxis = -> Sketch066 [N_Axis]
  Type = 0
FEATURE [Sketcher::SketchObject] Sketch067
  FullyConstrained = false
  MapMode = 5
  Placement = pos=(89.5,0,0) rot=(0.57735,0.57735,0.57735;2.0944rad)
  Support = -> [Pad001]
  sketch-geometry (4):
    g0: LineSegment StartX=10 StartY=25.3 StartZ=0 EndX=137 EndY=25.3 EndZ=0
    g1: LineSegment StartX=137 StartY=25.3 StartZ=0 EndX=137 EndY=22.3 EndZ=0
    g2: LineSegment StartX=137 StartY=22.3 StartZ=0 EndX=10 EndY=22.3 EndZ=0
    g3: LineSegment StartX=10 StartY=22.3 StartZ=0 EndX=10 EndY=25.3 EndZ=0
  constraints (10):
    c: Coincident(g0,g1)
    c: Coincident(g1,g2)
    c: Coincident(g2,g3)
    c: Coincident(g3,g0)
    c: Horizontal(g0)
    c: Horizontal(g2)
    c: Vertical(g1)
    c: Vertical(g3)
    c: DistanceX(g2,g2) = 127
    c: DistanceY(g1,g1) = 3
FEATURE [PartDesign::Pad] Pad002
  BaseFeature = -> Pad001
  Direction = (1,0,0)
  Length = 9
  Length2 = 10
  Profile = -> Sketch067
  ReferenceAxis = -> Sketch067 [N_Axis]
  Type = 0
FEATURE [Sketcher::SketchObject] Sketch068
  FullyConstrained = false
  MapMode = 5
  Support = -> [XY_Plane023]
  sketch-geometry (4):
    g0: LineSegment StartX=-157.3 StartY=140 StartZ=0 EndX=-44.5 EndY=140 EndZ=0
    g1: LineSegment StartX=-44.5 StartY=140 StartZ=0 EndX=-44.5 EndY=10 EndZ=0
    g2: LineSegment StartX=-44.5 StartY=10 StartZ=0 EndX=-157.3 EndY=10 EndZ=0
    g3: LineSegment StartX=-157.3 StartY=10 StartZ=0 EndX=-157.3 EndY=140 EndZ=0
  constraints (10):
    c: Coincident(g0,g1)
    c: Coincident(g1,g2)
    c: Coincident(g2,g3)
    c: Coincident(g3,g0)
    c: Horizontal(g0)
    c: Horizontal(g2)
    c: Vertical(g1)
    c: Vertical(g3)
    c: DistanceX(g0,g0) = 112.8
    c: DistanceY(g3,g3) = 130
FEATURE [PartDesign::Pad] Pad003
  Direction = (0,0,1)
  Length = 3
  Length2 = 10
  Profile = -> Sketch068
  ReferenceAxis = -> Sketch068 [N_Axis]
  Type = 0
FEATURE [Sketcher::SketchObject] Sketch069
  FullyConstrained = false
  MapMode = 5
  Placement = pos=(0,0,25.3) rot=(0,0,1;0rad)
  Support = -> [Pad002]
  sketch-geometry (21):
    g0: LineSegment StartX=-14.3 StartY=10 StartZ=0 EndX=-9.8 EndY=10 EndZ=0
    g1: LineSegment StartX=-9.8 StartY=10 StartZ=0 EndX=-9.8 EndY=137 EndZ=0
    g2: LineSegment StartX=-9.8 StartY=137 StartZ=0 EndX=-9.8 EndY=126.999 EndZ=0
    g3: LineSegment StartX=-9.8 StartY=126.999 StartZ=0 EndX=-9.8 EndY=100.25 EndZ=0
    g4: LineSegment StartX=-9.8 StartY=100.25 StartZ=0 EndX=-9.8 EndY=73.5 EndZ=0
    g5: LineSegment StartX=-9.8 StartY=73.5 StartZ=0 EndX=-9.8 EndY=46.7494 EndZ=0
    g6: Circle CenterX=-9.8 CenterY=20.0005 CenterZ=0 NormalX=0 NormalY=0 NormalZ=1 AngleXU=0 Radius=1.65
    g7: Circle CenterX=-9.8 CenterY=46.7494 CenterZ=0 NormalX=0 NormalY=0 NormalZ=1 AngleXU=0 Radius=1.65
    g8: Circle CenterX=-9.8 CenterY=73.5 CenterZ=0 NormalX=0 NormalY=0 NormalZ=1 AngleXU=0 Radius=1.65
    g9: Circle CenterX=-9.8 CenterY=100.25 CenterZ=0 NormalX=0 NormalY=0 NormalZ=1 AngleXU=0 Radius=1.65
    g10: Circle CenterX=-9.8 CenterY=126.999 CenterZ=0 NormalX=0 NormalY=0 NormalZ=1 AngleXU=0 Radius=1.65
    g11: LineSegment StartX=94 StartY=10.0008 StartZ=0 EndX=94 EndY=137.001 EndZ=0
    g12: LineSegment StartX=94 StartY=137.001 StartZ=0 EndX=94 EndY=127 EndZ=0
    g13: LineSegment StartX=94 StartY=127 StartZ=0 EndX=94 EndY=100.251 EndZ=0
    g14: LineSegment StartX=94 StartY=100.251 StartZ=0 EndX=94 EndY=73.5008 EndZ=0
    g15: LineSegment StartX=94 StartY=73.5008 StartZ=0 EndX=94 EndY=46.7503 EndZ=0
    g16: Circle CenterX=94 CenterY=20.0013 CenterZ=0 NormalX=0 NormalY=0 NormalZ=1 AngleXU=0 Radius=1.65
    g17: Circle CenterX=94 CenterY=46.7503 CenterZ=0 NormalX=0 NormalY=0 NormalZ=1 AngleXU=0 Radius=1.65
    g18: Circle CenterX=94 CenterY=73.5008 CenterZ=0 NormalX=0 NormalY=0 NormalZ=1 AngleXU=0 Radius=1.65
    g19: Circle CenterX=94 CenterY=100.251 CenterZ=0 NormalX=0 NormalY=0 NormalZ=1 AngleXU=0 Radius=1.65
    g20: Circle CenterX=94 CenterY=127 CenterZ=0 NormalX=0 NormalY=0 NormalZ=1 AngleXU=0 Radius=1.65
  constraints (36):
    c: Horizontal(g0)
    c: Coincident(g1,g0)
    c: Vertical(g1)
    c: Coincident(g2,g1)
    c: PointOnObject(g2,g1)
    c: Coincident(g3,g2)
    c: PointOnObject(g3,g1)
    c: Coincident(g3,g4)
    c: PointOnObject(g4,g1)
    c: Coincident(g4,g5)
    c: PointOnObject(g5,g1)
    c: PointOnObject(g6,g1)
    c: Coincident(g7,g5)
    c: Coincident(g8,g4)
    c: Coincident(g9,g3)
    c: Coincident(g10,g2)
    c: Vertical(g11)
    c: Coincident(g12,g11)
    c: PointOnObject(g12,g11)
    c: Coincident(g13,g12)
    c: PointOnObject(g13,g11)
    c: Coincident(g13,g14)
    c: PointOnObject(g14,g11)
    c: Coincident(g14,g15)
    c: PointOnObject(g15,g11)
    c: PointOnObject(g16,g11)
    c: Coincident(g17,g15)
    c: Coincident(g18,g14)
    c: Coincident(g19,g13)
    c: Coincident(g20,g12)
    c: Equal(g10,g9)
    c: Equal(g10,g8)
    c: Equal(g10,g7)
    c: Equal(g10,g6)
    c: Equal(g10, g16-g20) x5
    c: Diameter(g10) = 3.3
FEATURE [PartDesign::Pocket] Pocket014
  BaseFeature = -> Pad002
  Direction = (0,0,-1)
  Length = 5
  Length2 = 5
  Profile = -> Sketch069
  ReferenceAxis = -> Sketch069 [N_Axis]
  Type = 0
FEATURE [Sketcher::SketchObject] Sketch070
  FullyConstrained = false
  MapMode = 5
  Placement = pos=(0,0,3) rot=(0,0,1;0rad)
  Support = -> [Pad003]
  sketch-geometry (22):
    g0: LineSegment StartX=-157.3 StartY=10 StartZ=0 EndX=-152.8 EndY=10 EndZ=0
    g1: LineSegment StartX=-152.8 StartY=10 StartZ=0 EndX=-152.8 EndY=137 EndZ=0
    g2: LineSegment StartX=-152.8 StartY=137 StartZ=0 EndX=-152.8 EndY=126.999 EndZ=0
    g3: LineSegment StartX=-152.8 StartY=126.999 StartZ=0 EndX=-152.8 EndY=100.25 EndZ=0
    g4: LineSegment StartX=-152.8 StartY=100.25 StartZ=0 EndX=-152.8 EndY=73.5 EndZ=0
    g5: LineSegment StartX=-152.8 StartY=73.5 StartZ=0 EndX=-152.8 EndY=46.7494 EndZ=0
    g6: Circle CenterX=-152.8 CenterY=20.0005 CenterZ=0 NormalX=0 NormalY=0 NormalZ=1 AngleXU=0 Radius=1.65
    g7: Circle CenterX=-152.8 CenterY=46.7494 CenterZ=0 NormalX=0 NormalY=0 NormalZ=1 AngleXU=0 Radius=1.65
    g8: Circle CenterX=-152.8 CenterY=73.5 CenterZ=0 NormalX=0 NormalY=0 NormalZ=1 AngleXU=0 Radius=1.65
    g9: Circle CenterX=-152.8 CenterY=100.25 CenterZ=0 NormalX=0 NormalY=0 NormalZ=1 AngleXU=0 Radius=1.65
    g10: Circle CenterX=-152.8 CenterY=126.999 CenterZ=0 NormalX=0 NormalY=0 NormalZ=1 AngleXU=0 Radius=1.65
    g11: LineSegment StartX=-49 StartY=10.0008 StartZ=0 EndX=-49 EndY=137 EndZ=0
    g12: LineSegment StartX=-49 StartY=137 StartZ=0 EndX=-49 EndY=127 EndZ=0
    g13: LineSegment StartX=-49 StartY=127 StartZ=0 EndX=-49 EndY=100.251 EndZ=0
    g14: LineSegment StartX=-49 StartY=100.251 StartZ=0 EndX=-49 EndY=73.5008 EndZ=0
    g15: LineSegment StartX=-49 StartY=73.5008 StartZ=0 EndX=-49 EndY=46.7503 EndZ=0
    g16: Circle CenterX=-49 CenterY=20.0013 CenterZ=0 NormalX=0 NormalY=0 NormalZ=1 AngleXU=0 Radius=1.65
    g17: Circle CenterX=-49 CenterY=46.7503 CenterZ=0 NormalX=0 NormalY=0 NormalZ=1 AngleXU=0 Radius=1.65
    g18: Circle CenterX=-49 CenterY=73.5008 CenterZ=0 NormalX=0 NormalY=0 NormalZ=1 AngleXU=0 Radius=1.65
    g19: Circle CenterX=-49 CenterY=100.251 CenterZ=0 NormalX=0 NormalY=0 NormalZ=1 AngleXU=0 Radius=1.65
    g20: Circle CenterX=-49 CenterY=127 CenterZ=0 NormalX=0 NormalY=0 NormalZ=1 AngleXU=0 Radius=1.65
    g21: LineSegment StartX=-152.8 StartY=137 StartZ=0 EndX=-49 EndY=137 EndZ=0
  constraints (43):
    c: Horizontal(g0)
    c: Coincident(g1,g0)
    c: Vertical(g1)
    c: Coincident(g2,g1)
    c: PointOnObject(g2,g1)
    c: Coincident(g3,g2)
    c: PointOnObject(g3,g1)
    c: Coincident(g3,g4)
    c: PointOnObject(g4,g1)
    c: Coincident(g4,g5)
    c: PointOnObject(g5,g1)
    c: PointOnObject(g6,g1)
    c: Coincident(g7,g5)
    c: Coincident(g8,g4)
    c: Coincident(g9,g3)
    c: Coincident(g10,g2)
    c: Vertical(g11)
    c: Coincident(g12,g11)
    c: PointOnObject(g12,g11)
    c: Coincident(g13,g12)
    c: PointOnObject(g13,g11)
    c: Coincident(g13,g14)
    c: PointOnObject(g14,g11)
    c: Coincident(g14,g15)
    c: PointOnObject(g15,g11)
    c: PointOnObject(g16,g11)
    c: Coincident(g17,g15)
    c: Coincident(g18,g14)
    c: Coincident(g19,g13)
    c: Coincident(g20,g12)
    c: Equal(g10,g9)
    c: Equal(g10,g8)
    c: Equal(g10,g7)
    c: Equal(g10,g6)
    c: Equal(g10, g16-g20) x5
    c: Diameter(g10) = 3.3
    c: Coincident(g21,g1)
    c: Coincident(g21,g11)
    c: Horizontal(g21)
    c: DistanceX(g21,g21) = 103.8
    c: DistanceX(g0,g0) = 4.5
    c: Distance(g1) = 127
    c: Distance(g11) = 126.999
FEATURE [PartDesign::Hole] Hole015
  BaseFeature = -> Pad003
  CustomThreadClearance = 0
  Depth = 3
  DepthType = 0
  Diameter = 3.3
  DrillForDepth = false
  DrillPoint = 0
  DrillPointAngle = 118
  HoleCutCountersinkAngle = 90
  HoleCutCustomValues = false
  HoleCutDepth = 2
  HoleCutDiameter = 5.6
  HoleCutType = 2
  ModelThread = false
  Profile = -> Sketch070
  Tapered = false
  TaperedAngle = 90
  ThreadClass = 0
  ThreadDepth = 3
  ThreadDepthType = 0
  ThreadDirection = 0
  ThreadFit = 0
  ThreadSize = 0
  ThreadType = 0
  Threaded = false
  UseCustomThreadClearance = false
FEATURE [Sketcher::SketchObject] Sketch072
  FullyConstrained = false
  MapMode = 5
  Placement = pos=(0,10,0) rot=(1,0,0;1.5708rad)
  Support = -> [Pocket014]
  sketch-geometry (4):
    g0: LineSegment StartX=-3.3 StartY=2.01 StartZ=0 EndX=87.5 EndY=2.01 EndZ=0
    g1: LineSegment StartX=87.5 StartY=2.01 StartZ=0 EndX=87.5 EndY=1.81 EndZ=0
    g2: LineSegment StartX=87.5 StartY=1.81 StartZ=0 EndX=-3.3 EndY=1.81 EndZ=0
    g3: LineSegment StartX=-3.3 StartY=1.81 StartZ=0 EndX=-3.3 EndY=2.01 EndZ=0
  constraints (10):
    c: Coincident(g0,g1)
    c: Coincident(g1,g2)
    c: Coincident(g2,g3)
    c: Coincident(g3,g0)
    c: Horizontal(g0)
    c: Horizontal(g2)
    c: Vertical(g1)
    c: Vertical(g3)
    c: DistanceX(g0,g0) = 90.8
    c: DistanceY(g1,g1) = 0.2
FEATURE [PartDesign::Pocket] Pocket015
  BaseFeature = -> Pocket014
  Direction = (0,1,-2e-16)
  Length = 100
  Length2 = 5
  Profile = -> Sketch072
  ReferenceAxis = -> Sketch072 [N_Axis]
  Type = 0
FEATURE [Sketcher::SketchObject] Sketch073
  FullyConstrained = false
  MapMode = 5
  Placement = pos=(0,0,3) rot=(0,0,1;0rad)
  Support = -> [Hole015]
  sketch-geometry (7):
    g0: LineSegment StartX=-106.14 StartY=18.59 StartZ=0 EndX=-95.54 EndY=18.59 EndZ=0
    g1: LineSegment StartX=-95.54 StartY=18.59 StartZ=0 EndX=-95.54 EndY=12.99 EndZ=0
    g2: LineSegment StartX=-95.54 StartY=12.99 StartZ=0 EndX=-106.14 EndY=12.99 EndZ=0
    g3: LineSegment StartX=-106.14 StartY=12.99 StartZ=0 EndX=-106.14 EndY=18.59 EndZ=0
    g4: LineSegment StartX=-106.14 StartY=12.99 StartZ=0 EndX=-106.14 EndY=10 EndZ=0
    g5: LineSegment StartX=-106.14 StartY=12.99 StartZ=0 EndX=-148.3 EndY=12.99 EndZ=0
    g6: LineSegment StartX=-148.3 StartY=12.99 StartZ=0 EndX=-157.3 EndY=12.99 EndZ=0
  constraints (19):
    c: Coincident(g0,g1)
    c: Coincident(g1,g2)
    c: Coincident(g2,g3)
    c: Coincident(g3,g0)
    c: Horizontal(g0)
    c: Horizontal(g2)
    c: Vertical(g1)
    c: Vertical(g3)
    c: DistanceX(g2,g2) = 10.6
    c: DistanceY(g1,g1) = 5.6
    c: Coincident(g4,g2)
    c: Vertical(g4)
    c: Coincident(g5,g2)
    c: Horizontal(g5)
    c: DistanceX(g5,g5) = 42.16
    c: DistanceY(g4,g4) = 2.99
    c: Coincident(g6,g5)
    c: Horizontal(g6)
    c: DistanceX(g6,g6) = 9
FEATURE [PartDesign::Pocket] Pocket016
  BaseFeature = -> Hole015
  Direction = (0,0,-1)
  Length = 5
  Length2 = 5
  Profile = -> Sketch073
  ReferenceAxis = -> Sketch073 [N_Axis]
  Type = 0
FEATURE [Sketcher::SketchObject] Sketch074
  FullyConstrained = false
  MapMode = 5
  Placement = pos=(84.5,0,0) rot=(0.57735,-0.57735,-0.57735;2.0944rad)
  Support = -> [Pocket015]
  sketch-geometry (3):
    g0: LineSegment StartX=-10 StartY=30.3 StartZ=0 EndX=-10 EndY=18.05 EndZ=0
    g1: LineSegment StartX=-10 StartY=18.05 StartZ=0 EndX=-33.375 EndY=18.05 EndZ=0
    g2: Circle CenterX=-33.375 CenterY=18.05 CenterZ=0 NormalX=0 NormalY=0 NormalZ=1 AngleXU=0 Radius=1.65
  constraints (7):
    c: Vertical(g0)
    c: DistanceY(g0,g0) = 12.25
    c: Coincident(g1,g0)
    c: Horizontal(g1)
    c: DistanceX(g1,g1) = 23.375
    c: Coincident(g2,g1)
    c: Diameter(g2) = 3.3
FEATURE [PartDesign::Hole] Hole016
  BaseFeature = -> Pocket015
  CustomThreadClearance = 0
  Depth = 5
  DepthType = 0
  Diameter = 3.3
  DrillForDepth = false
  DrillPoint = 0
  DrillPointAngle = 118
  HoleCutCountersinkAngle = 90
  HoleCutCustomValues = false
  HoleCutDepth = 3
  HoleCutDiameter = 6
  HoleCutType = 2
  ModelThread = false
  Profile = -> Sketch074
  Tapered = false
  TaperedAngle = 90
  ThreadClass = 0
  ThreadDepth = 5
  ThreadDepthType = 0
  ThreadDirection = 0
  ThreadFit = 0
  ThreadSize = 0
  ThreadType = 0
  Threaded = false
  UseCustomThreadClearance = false
FEATURE [Sketcher::SketchObject] Sketch075
  FullyConstrained = false
  MapMode = 5
  Placement = pos=(0,0,0) rot=(0.57735,0.57735,0.57735;2.0944rad)
  sketch-geometry (3):
    g0: LineSegment StartX=33.3743 StartY=30.6056 StartZ=0 EndX=33.3743 EndY=18.3556 EndZ=0
    g1: LineSegment StartX=33.3743 StartY=18.3556 StartZ=0 EndX=9.99927 EndY=18.3556 EndZ=0
    g2: Circle CenterX=33.3743 CenterY=18.3556 CenterZ=0 NormalX=0 NormalY=0 NormalZ=1 AngleXU=0 Radius=1.65
  constraints (7):
    c: Vertical(g0)
    c: DistanceY(g0,g0) = 12.25
    c: Coincident(g1,g0)
    c: Horizontal(g1)
    c: DistanceX(g1,g1) = 23.375
    c: Coincident(g2,g0)
    c: Diameter(g2) = 3.3
FEATURE [PartDesign::Hole] Hole017
  BaseFeature = -> Hole016
  CustomThreadClearance = 0
  Depth = 5.3
  DepthType = 0
  Diameter = 3.5
  DrillForDepth = false
  DrillPoint = 0
  DrillPointAngle = 118
  HoleCutCountersinkAngle = 90
  HoleCutCustomValues = false
  HoleCutDepth = 3
  HoleCutDiameter = 6
  HoleCutType = 2
  ModelThread = false
  Profile = -> Sketch075
  Tapered = false
  TaperedAngle = 90
  ThreadClass = 0
  ThreadDepth = 5.3
  ThreadDepthType = 0
  ThreadDirection = 0
  ThreadFit = 0
  ThreadSize = 0
  ThreadType = 0
  Threaded = false
  UseCustomThreadClearance = false
FEATURE [PartDesign::Fillet] Fillet
  Base = -> Hole017 [Edge117,Edge114]
  BaseFeature = -> Hole017
  Radius = 3.35
  SupportTransform = false
  UseAllEdges = false
FEATURE [PartDesign::Fillet] Fillet001
  Base = -> Pocket016 [Edge2,Edge1]
  BaseFeature = -> Pocket016
  Radius = 3.35
  SupportTransform = false
  UseAllEdges = false
FEATURE [PartDesign::Body] Body009  label="sleeve enclosure top plate"
  Group = -> [Sketch068,Pad003,Sketch070,Hole015,Sketch073,Pocket016,Fillet001]
  Origin = -> Origin023
  Placement = pos=(0,0,25.3) rot=(0,0,1;0rad)
  Tip = -> Fillet001
FEATURE [PartDesign::Fillet] Fillet002
  Base = -> Fillet [Edge23,Edge40]
  BaseFeature = -> Fillet
  Radius = 3.35
  SupportTransform = false
  UseAllEdges = false
FEATURE [Sketcher::SketchObject] Sketch076
  FullyConstrained = false
  MapMode = 5
  Placement = pos=(0,112,0) rot=(0,0.707107,0.707107;3.14159rad)
  Support = -> [Fillet002]
  sketch-geometry (4):
    g0: LineSegment StartX=-24.82 StartY=16.3 StartZ=0 EndX=-6.82 EndY=16.3 EndZ=0
    g1: LineSegment StartX=-6.82 StartY=16.3 StartZ=0 EndX=-6.82 EndY=12.3 EndZ=0
    g2: LineSegment StartX=-6.82 StartY=12.3 StartZ=0 EndX=-24.82 EndY=12.3 EndZ=0
    g3: LineSegment StartX=-24.82 StartY=12.3 StartZ=0 EndX=-24.82 EndY=16.3 EndZ=0
  constraints (10):
    c: Coincident(g0,g1)
    c: Coincident(g1,g2)
    c: Coincident(g2,g3)
    c: Coincident(g3,g0)
    c: Horizontal(g0)
    c: Horizontal(g2)
    c: Vertical(g1)
    c: Vertical(g3)
    c: DistanceX(g0,g0) = 18
    c: DistanceY(g3,g3) = 4
FEATURE [PartDesign::Pocket] Pocket017
  BaseFeature = -> Fillet002
  Direction = (0,-1,2e-16)
  Length = 2
  Length2 = 5
  Profile = -> Sketch076
  ReferenceAxis = -> Sketch076 [N_Axis]
  Type = 0
FEATURE [PartDesign::Body] Body008  label="sleeve enclosure v2"
  Group = -> [Sketch062,Pad,Sketch063,Pocket011,Sketch064,Pocket012,Sketch065,Pocket013,Sketch066,Pad001,Sketch067,Pad002,Sketch069,Pocket014,Sketch072,Pocket015,Sketch074,Hole016,Sketch075,Hole017,Fillet,Fillet002,Sketch076,Pocket017]
  Origin = -> Origin021
  Placement = pos=(-143,0,0) rot=(0,0,1;0rad)
  Tip = -> Pocket017
FEATURE [App::Part] Part013  label="batt sleeve v2"
  Group = -> [Body008,Body009]
  Origin = -> Origin022
FEATURE [App::MeasureDistance] Distance021  label="Distance: 94.80000 mm001"
  Distance = 94.8
  P1 = (-5.3,-6e-15,26.19)
  P2 = (89.5,-6e-15,26.19)
FEATURE [App::MeasureDistance] Distance022  label="Distance: 127.00000 mm"
  Distance = 127
  P1 = (-5.3,-6e-15,26.19)
  P2 = (-5.3,-127,26.19)
FEATURE [App::MeasureDistance] Distance023  label="Distance: 3.11000 mm"
  Distance = 3.11
  P1 = (-0.300001,-127,23.08)
  P2 = (-0.295033,-127,26.19)
FEATURE [App::MeasureDistance] Distance024  label="Distance: 2.00000 mm"
  Distance = 2
  P1 = (-0.0360109,-127,-0.3)
  P2 = (-0.0360109,-127,-2.3)
FEATURE [App::MeasureDistance] Distance025  label="Distance: 5.00890 mm"
  Distance = 5.0089
  P1 = (-0.300001,-127,23.08)
  P2 = (-5.3,-127,22.7815)
